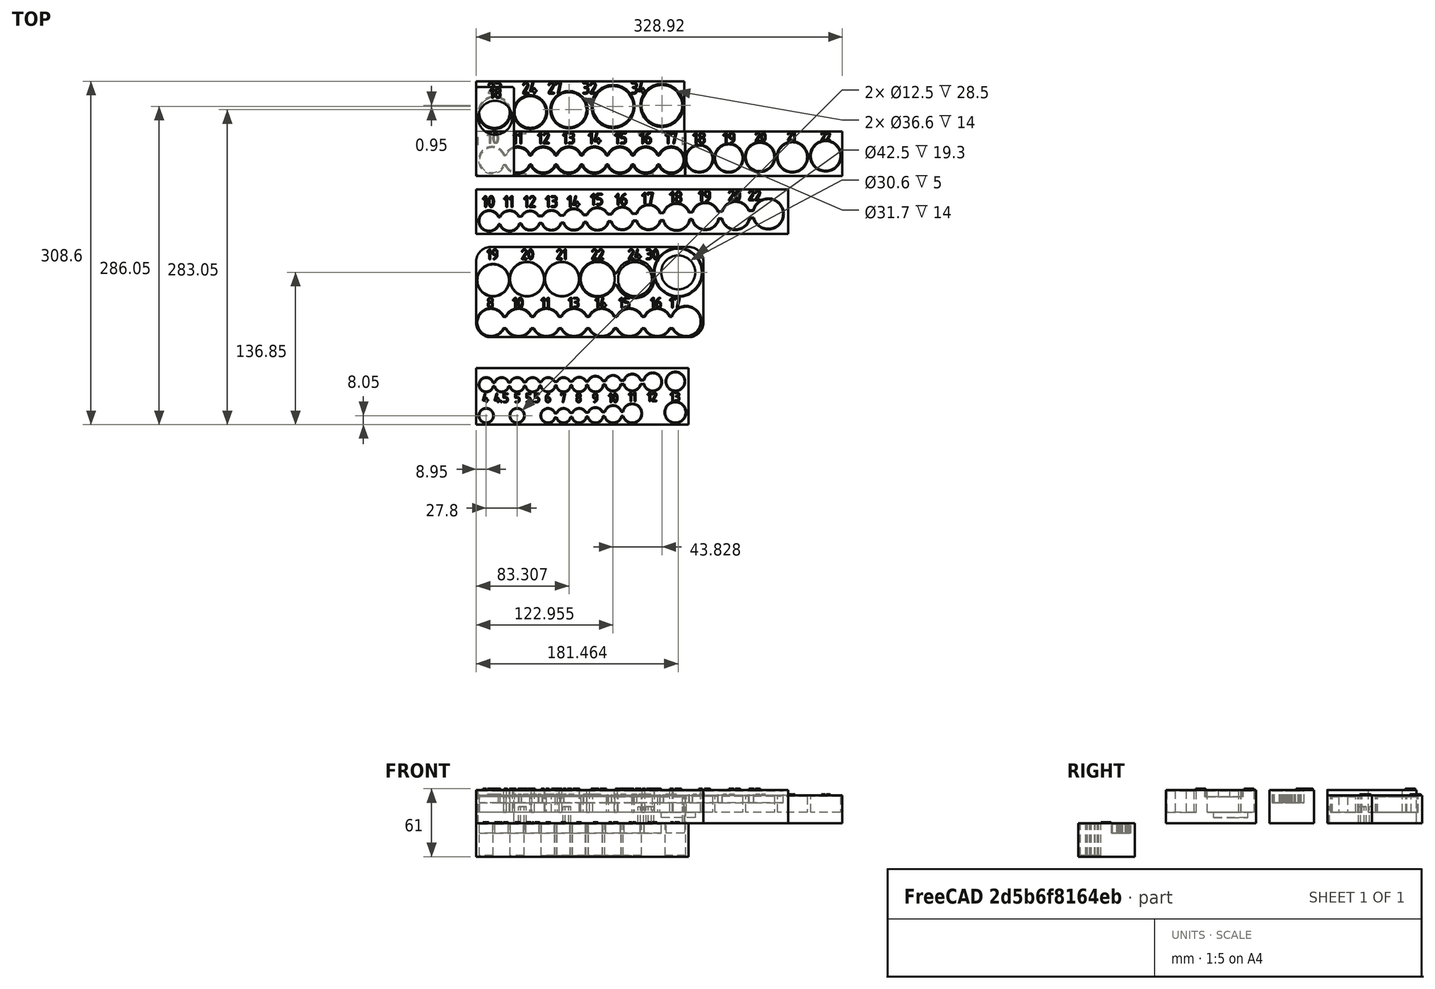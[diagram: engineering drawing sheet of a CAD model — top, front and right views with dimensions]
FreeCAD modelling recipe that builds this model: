
FCSTD DOCUMENT  (FreeCAD 1.1R44227 +568 (Git))
Label: Socket_organizer
License: All rights reserved
LicenseURL: https://en.wikipedia.org/wiki/All_rights_reserved
objects: PartDesign::Pad×64, Part::Part2DObjectPython×57, Sketcher::SketchObject×19, PartDesign::Pocket×15, PartDesign::Chamfer×7, PartDesign::Body×7, App::Point×7, PartDesign::Fillet×3
note: 369 computed .brp shape members not serialized (recipe doc carries the construction recipe); baked Part::Feature solids carry a one-line shape summary decoded from their .brp

FEATURE [Sketcher::SketchObject] Sketch001
  ArcFitTolerance = 1e-06
  ExternalTypes = [0]
  FullyConstrained = true
  MakeInternals = false
  MapMode = 5
  Placement = pos=(0,0,25) rot=(0,0,1;0rad)
  _ExternalGeoVersion = 0
  sketch-geometry (42):
    g0: LineSegment [constr] StartX=14.25 StartY=3 StartZ=0 EndX=14.25 EndY=0 EndZ=0
    g1: LineSegment [constr] StartX=3 StartY=14.25 StartZ=0 EndX=0 EndY=14.25 EndZ=0
    g2: ArcOfCircle CenterX=14.25 CenterY=14.25 CenterZ=0 NormalX=0 NormalY=0 NormalZ=1 AngleXU=0 Radius=11.25 StartAngle=0.363508 EndAngle=5.91968
    g3: LineSegment StartX=24.7649 StartY=18.25 StartZ=0 EndX=26.7351 EndY=18.25 EndZ=0
    g4: LineSegment StartX=24.7649 StartY=10.25 StartZ=0 EndX=26.7351 EndY=10.25 EndZ=0
    g5: ArcOfCircle CenterX=37.25 CenterY=14.25 CenterZ=0 NormalX=0 NormalY=0 NormalZ=1 AngleXU=0 Radius=11.25 StartAngle=0.363508 EndAngle=2.77808
    g6: ArcOfCircle CenterX=37.25 CenterY=14.25 CenterZ=0 NormalX=0 NormalY=0 NormalZ=1 AngleXU=0 Radius=11.25 StartAngle=3.5051 EndAngle=5.91968
    g7: ArcOfCircle CenterX=60.25 CenterY=14.25 CenterZ=0 NormalX=0 NormalY=0 NormalZ=1 AngleXU=0 Radius=11.25 StartAngle=0.363508 EndAngle=2.77808
    g8: ArcOfCircle CenterX=60.25 CenterY=14.25 CenterZ=0 NormalX=0 NormalY=0 NormalZ=1 AngleXU=0 Radius=11.25 StartAngle=3.5051 EndAngle=5.91968
    g9: ArcOfCircle CenterX=83.25 CenterY=14.25 CenterZ=0 NormalX=0 NormalY=0 NormalZ=1 AngleXU=0 Radius=11.25 StartAngle=0.363508 EndAngle=2.77808
    g10: ArcOfCircle CenterX=83.25 CenterY=14.25 CenterZ=0 NormalX=0 NormalY=0 NormalZ=1 AngleXU=0 Radius=11.25 StartAngle=3.5051 EndAngle=5.91968
    g11: ArcOfCircle CenterX=106.25 CenterY=14.25 CenterZ=0 NormalX=0 NormalY=0 NormalZ=1 AngleXU=0 Radius=11.25 StartAngle=0.363508 EndAngle=2.77808
    g12: ArcOfCircle CenterX=106.25 CenterY=14.25 CenterZ=0 NormalX=0 NormalY=0 NormalZ=1 AngleXU=0 Radius=11.25 StartAngle=3.5051 EndAngle=5.91968
    g13: LineSegment StartX=49.7351 StartY=18.25 StartZ=0 EndX=47.7649 EndY=18.25 EndZ=0
    g14: LineSegment StartX=49.7351 StartY=10.25 StartZ=0 EndX=47.7649 EndY=10.25 EndZ=0
    g15: LineSegment StartX=72.7351 StartY=18.25 StartZ=0 EndX=70.7649 EndY=18.25 EndZ=0
    g16: LineSegment StartX=72.7351 StartY=10.25 StartZ=0 EndX=70.7649 EndY=10.25 EndZ=0
    g17: LineSegment StartX=95.7351 StartY=18.25 StartZ=0 EndX=93.7649 EndY=18.25 EndZ=0
    g18: LineSegment StartX=95.7351 StartY=10.25 StartZ=0 EndX=93.7649 EndY=10.25 EndZ=0
    g19: ArcOfCircle CenterX=129.25 CenterY=14.25 CenterZ=0 NormalX=0 NormalY=0 NormalZ=1 AngleXU=0 Radius=11.25 StartAngle=0.363508 EndAngle=2.77808
    g20: ArcOfCircle CenterX=152.25 CenterY=14.25 CenterZ=0 NormalX=0 NormalY=0 NormalZ=1 AngleXU=0 Radius=11.25 StartAngle=0.363508 EndAngle=2.77808
    g21: ArcOfCircle CenterX=129.25 CenterY=14.25 CenterZ=0 NormalX=0 NormalY=0 NormalZ=1 AngleXU=0 Radius=11.25 StartAngle=3.5051 EndAngle=5.91968
    g22: ArcOfCircle CenterX=152.25 CenterY=14.25 CenterZ=0 NormalX=0 NormalY=0 NormalZ=1 AngleXU=0 Radius=11.25 StartAngle=3.5051 EndAngle=5.91968
    g23: LineSegment StartX=164.735 StartY=18.25 StartZ=0 EndX=162.765 EndY=18.25 EndZ=0
    g24: LineSegment StartX=164.735 StartY=10.25 StartZ=0 EndX=162.765 EndY=10.25 EndZ=0
    g25: LineSegment StartX=116.765 StartY=10.25 StartZ=0 EndX=118.735 EndY=10.25 EndZ=0
    g26: LineSegment StartX=118.735 StartY=18.25 StartZ=0 EndX=116.765 EndY=18.25 EndZ=0
    g27: LineSegment StartX=139.765 StartY=18.25 StartZ=0 EndX=141.735 EndY=18.25 EndZ=0
    g28: LineSegment StartX=141.735 StartY=10.25 StartZ=0 EndX=139.765 EndY=10.25 EndZ=0
    g29: ArcOfCircle CenterX=175.25 CenterY=14.25 CenterZ=0 NormalX=0 NormalY=0 NormalZ=1 AngleXU=0 Radius=11.25 StartAngle=3.5051 EndAngle=9.06127
    g30: LineSegment [constr] StartX=14.25 StartY=14.25 StartZ=0 EndX=37.25 EndY=14.25 EndZ=0
    g31: LineSegment [constr] StartX=37.25 StartY=14.25 StartZ=0 EndX=60.25 EndY=14.25 EndZ=0
    g32: LineSegment [constr] StartX=60.25 StartY=14.25 StartZ=0 EndX=83.25 EndY=14.25 EndZ=0
    g33: LineSegment [constr] StartX=83.25 StartY=14.25 StartZ=0 EndX=106.25 EndY=14.25 EndZ=0
    g34: LineSegment [constr] StartX=106.25 StartY=14.25 StartZ=0 EndX=129.25 EndY=14.25 EndZ=0
    g35: LineSegment [constr] StartX=152.25 StartY=14.25 StartZ=0 EndX=129.25 EndY=14.25 EndZ=0
    g36: LineSegment [constr] StartX=152.25 StartY=14.25 StartZ=0 EndX=175.25 EndY=14.25 EndZ=0
    g37: LineSegment StartX=0 StartY=0 StartZ=0 EndX=187.5 EndY=0 EndZ=0
    g38: LineSegment StartX=187.5 StartY=0 StartZ=0 EndX=187.5 EndY=40 EndZ=0
    g39: LineSegment StartX=187.5 StartY=40 StartZ=0 EndX=0 EndY=40 EndZ=0
    g40: LineSegment StartX=0 StartY=40 StartZ=0 EndX=0 EndY=0 EndZ=0
    g41: LineSegment [constr] StartX=187.5 StartY=14.25 StartZ=0 EndX=186.5 EndY=14.25 EndZ=0
  constraints (129):
    c: PointOnObject(g0,g-1)
    c: Vertical(g0)
    c: PointOnObject(g1,g-2)
    c: Horizontal(g1)
    c: Equal(g0,g1)
    c: DistanceY(g0,g0) = 3
    c: PointOnObject(g1,g2)
    c: PointOnObject(g0,g2)
    c: Perpendicular(g2,g0)
    c: Perpendicular(g2,g1)
    c: Coincident(g3,g2)
    c: Horizontal(g3)
    c: Coincident(g4,g2)
    c: Horizontal(g4)
    c: Coincident(g5,g3)
    c: Coincident(g6,g5)
    c: Coincident(g6,g4)
    c: Coincident(g8,g7)
    c: Coincident(g10,g9)
    c: Coincident(g12,g11)
    c: Coincident(g13,g7)
    c: Coincident(g13,g5)
    c: Coincident(g14,g8)
    c: Coincident(g14,g6)
    c: Horizontal(g14)
    c: Coincident(g15,g9)
    c: Coincident(g15,g7)
    c: Coincident(g16,g10)
    c: Coincident(g16,g8)
    c: Coincident(g17,g11)
    c: Coincident(g17,g9)
    c: Coincident(g18,g12)
    c: Coincident(g18,g10)
    c: Coincident(g21,g19)
    c: Coincident(g22,g20)
    c: Equal(g20,g19)
    c: Equal(g19,g11)
    c: Equal(g11,g9)
    c: Equal(g9,g7)
    c: Equal(g7,g5)
    c: Equal(g5,g2)
    c: Equal(g2,g6)
    c: Equal(g6,g8)
    c: Equal(g8,g10)
    c: Equal(g10,g12)
    c: Equal(g12,g21)
    c: Equal(g21,g22)
    c: Coincident(g23,g20)
    c: Coincident(g24,g22)
    c: Coincident(g25,g12)
    c: Coincident(g25,g21)
    c: Coincident(g26,g19)
    c: Coincident(g26,g11)
    c: Diameter(g2) = 22.5
    c: Horizontal(g24)
    c: Horizontal(g23)
    c: Coincident(g27,g19)
    c: Coincident(g27,g20)
    c: Coincident(g28,g22)
    c: Coincident(g28,g21)
    c: Horizontal(g28)
    c: Horizontal(g27)
    c: Horizontal(g25)
    c: Horizontal(g26)
    c: Horizontal(g18)
    c: Horizontal(g17)
    c: Horizontal(g15)
    c: Horizontal(g16)
    c: Horizontal(g13)
    c: Horizontal(g20,g19)
    c: Horizontal(g19,g11)
    c: Horizontal(g11,g9)
    c: Horizontal(g9,g7)
    c: Horizontal(g7,g5)
    c: Horizontal(g5,g2)
    c: Horizontal(g22,g21)
    c: Horizontal(g21,g12)
    c: Horizontal(g12,g10)
    c: Horizontal(g10,g8)
    c: Horizontal(g8,g6)
    c: Horizontal(g6,g2)
    c: Horizontal(g20,g19)
    c: Horizontal(g19,g11)
    c: Horizontal(g11,g9)
    c: Horizontal(g9,g7)
    c: Horizontal(g7,g5)
    c: Horizontal(g5,g2)
    c: Coincident(g29,g23)
    c: Coincident(g29,g24)
    c: Horizontal(g29,g20)
    c: DistanceY(g2,g2) = 4
    c: DistanceY(g2,g2) = 4
    c: Coincident(g30,g2)
    c: Coincident(g30,g5)
    c: Coincident(g31,g5)
    c: Coincident(g31,g7)
    c: Coincident(g32,g7)
    c: Coincident(g32,g9)
    c: Coincident(g33,g9)
    c: Coincident(g33,g11)
    c: Coincident(g34,g11)
    c: Coincident(g34,g19)
    c: Coincident(g35,g20)
    c: Coincident(g35,g19)
    c: Coincident(g36,g20)
    c: Coincident(g36,g29)
    c: Equal(g36,g35)
    c: Equal(g35,g34)
    c: Equal(g34,g33)
    c: Equal(g33,g32)
    c: Equal(g32,g31)
    c: Equal(g31,g30)
    c: Equal(g29,g22)
    c: DistanceX(g30,g30) = 23
    c: Coincident(g37,g38)
    c: Coincident(g38,g39)
    c: Coincident(g39,g40)
    c: Coincident(g40,g37)
    c: Horizontal(g37)
    c: Horizontal(g39)
    c: Vertical(g38)
    c: Vertical(g40)
    c: Coincident(g37,g-1)
    c: DistanceY(g40,g40) = 40
    c: PointOnObject(g41,g38)
    c: PointOnObject(g41,g29)
    c: Horizontal(g41)
    c: Perpendicular(g29,g41)
    c: DistanceX(g41,g41) = 1
FEATURE [PartDesign::Pad] Pad
  Direction = (0,0,1)
  Length = 25
  Length2 = 10
  Placement = pos=(0,0,25) rot=(0,0,1;0rad)
  Profile = -> Sketch001 [Edge32,Edge29,Edge31,Edge30]
  ReferenceAxis = -> Sketch001 [N_Axis]
  Refine = true
  Reversed = true
  SideType = 0
  Suppressed = false
  Type = 0
  Type2 = 0
FEATURE [PartDesign::Pocket] Pocket
  BaseFeature = -> Pad
  Direction = (0,0,-1)
  Length = 15
  Length2 = 5
  Placement = pos=(0,0,25) rot=(0,0,1;0rad)
  Profile = -> Sketch001 [Edge13,Edge12,Edge10,Edge11,Edge9,Vertex8,Edge8,Edge7,Edge14,Edge15,Edge17,Vertex17,Edge16,Edge6,Edge5,Edge4,Edge18,Edge19,Edge3,Edge2,Edge20,Edge21,Edge1,Edge22,Edge28,Edge27,Edge23,Edge25,Edge24,Edge26]
  ReferenceAxis = -> Sketch001 [N_Axis]
  Refine = true
  SideType = 0
  Suppressed = false
  Type = 0
  Type2 = 0
FEATURE [Sketcher::SketchObject] Sketch
  ArcFitTolerance = 1e-06
  AttachmentSupport = -> [XY_Plane001]
  ExternalTypes = [0]
  FullyConstrained = true
  MakeInternals = false
  MapMode = 5
  _ExternalGeoVersion = 0
  sketch-geometry (25):
    g0: LineSegment StartX=0 StartY=0 StartZ=0 EndX=140.921 EndY=0 EndZ=0
    g1: LineSegment StartX=140.921 StartY=0 StartZ=0 EndX=140.921 EndY=40 EndZ=0
    g2: LineSegment StartX=140.921 StartY=40 StartZ=0 EndX=0 EndY=40 EndZ=0
    g3: LineSegment StartX=0 StartY=40 StartZ=0 EndX=0 EndY=0 EndZ=0
    g4: Circle CenterX=12.5 CenterY=15.5 CenterZ=0 NormalX=0 NormalY=0 NormalZ=1 AngleXU=0 Radius=11.8
    g5: Circle CenterX=38.9904 CenterY=16 CenterZ=0 NormalX=0 NormalY=0 NormalZ=1 AngleXU=0 Radius=12.35
    g6: Circle CenterX=67.0011 CenterY=17.05 CenterZ=0 NormalX=0 NormalY=0 NormalZ=1 AngleXU=0 Radius=12.8
    g7: Circle CenterX=96.051 CenterY=17 CenterZ=0 NormalX=0 NormalY=0 NormalZ=1 AngleXU=0 Radius=13.25
    g8: Circle CenterX=125.971 CenterY=17.95 CenterZ=0 NormalX=0 NormalY=0 NormalZ=1 AngleXU=0 Radius=13.3
    g9: Circle [constr] CenterX=12.5 CenterY=15.5 CenterZ=0 NormalX=0 NormalY=0 NormalZ=1 AngleXU=0 Radius=12.5
    g10: Circle [constr] CenterX=38.9904 CenterY=16 CenterZ=0 NormalX=0 NormalY=0 NormalZ=1 AngleXU=0 Radius=13
    g11: Circle [constr] CenterX=67.0011 CenterY=17.05 CenterZ=0 NormalX=0 NormalY=0 NormalZ=1 AngleXU=0 Radius=14.05
    g12: Circle [constr] CenterX=96.051 CenterY=17 CenterZ=0 NormalX=0 NormalY=0 NormalZ=1 AngleXU=0 Radius=14
    g13: Circle [constr] CenterX=125.971 CenterY=17.95 CenterZ=0 NormalX=0 NormalY=0 NormalZ=1 AngleXU=0 Radius=14.95
    g14: LineSegment [constr] StartX=12.5 StartY=3 StartZ=0 EndX=12.5 EndY=0 EndZ=0
    g15: LineSegment [constr] StartX=38.9904 StartY=3 StartZ=0 EndX=38.9904 EndY=0 EndZ=0
    g16: LineSegment [constr] StartX=67.0011 StartY=3 StartZ=0 EndX=67.0011 EndY=0 EndZ=0
    g17: LineSegment [constr] StartX=96.051 StartY=3 StartZ=0 EndX=96.051 EndY=0 EndZ=0
    g18: LineSegment [constr] StartX=125.971 StartY=3 StartZ=0 EndX=125.971 EndY=0 EndZ=0
    g19: LineSegment [constr] StartX=25 StartY=15.5 StartZ=0 EndX=26 EndY=15.5 EndZ=0
    g20: LineSegment [constr] StartX=51.9904 StartY=16 StartZ=0 EndX=52.9904 EndY=16 EndZ=0
    g21: LineSegment [constr] StartX=81.0511 StartY=17.05 StartZ=0 EndX=82.0511 EndY=17.05 EndZ=0
    g22: LineSegment [constr] StartX=110.051 StartY=17 StartZ=0 EndX=111.051 EndY=17 EndZ=0
    g23: GeomPoint [constr] X=0 Y=15.5 Z=0
    g24: GeomPoint [constr] X=140.921 Y=17.95 Z=0
  constraints (76):
    c: Coincident(g0,g1)
    c: Coincident(g1,g2)
    c: Coincident(g2,g3)
    c: Coincident(g3,g0)
    c: Horizontal(g0)
    c: Horizontal(g2)
    c: Vertical(g1)
    c: Vertical(g3)
    c: Coincident(g0,g-1)
    c: Diameter(g4) = 23.6
    c: Diameter(g5) = 24.7
    c: Diameter(g6) = 25.6
    c: Diameter(g7) = 26.5
    c: Diameter(g8) = 26.6
    c: Coincident(g9,g4)
    c: Coincident(g10,g5)
    c: Coincident(g11,g6)
    c: Coincident(g12,g7)
    c: Coincident(g13,g8)
    c: Diameter(g9) = 25
    c: Diameter(g10) = 26
    c: Diameter(g11) = 28.1
    c: Diameter(g12) = 28
    c: Diameter(g13) = 29.9
    c: PointOnObject(g14,g9)
    c: PointOnObject(g14,g0)
    c: Vertical(g14)
    c: PointOnObject(g15,g10)
    c: PointOnObject(g15,g0)
    c: Vertical(g15)
    c: PointOnObject(g16,g11)
    c: PointOnObject(g16,g0)
    c: PointOnObject(g17,g12)
    c: PointOnObject(g17,g0)
    c: Vertical(g17)
    c: PointOnObject(g18,g13)
    c: PointOnObject(g18,g0)
    c: Vertical(g18)
    c: Perpendicular(g13,g18)
    c: Perpendicular(g12,g17)
    c: Vertical(g16)
    c: Perpendicular(g11,g16)
    c: Perpendicular(g10,g15)
    c: Perpendicular(g9,g14)
    c: Equal(g14,g15)
    c: Equal(g15,g16)
    c: Equal(g16,g17)
    c: Equal(g17,g18)
    c: DistanceY(g14,g14) = 3
    c: PointOnObject(g19,g9)
    c: PointOnObject(g19,g10)
    c: Horizontal(g19)
    c: Perpendicular(g9,g19)
    c: PointOnObject(g20,g10)
    c: PointOnObject(g20,g11)
    c: Horizontal(g20)
    c: Perpendicular(g10,g20)
    c: PointOnObject(g21,g11)
    c: PointOnObject(g21,g12)
    c: Horizontal(g21)
    c: Perpendicular(g11,g21)
    c: PointOnObject(g22,g12)
    c: PointOnObject(g22,g13)
    c: Horizontal(g22)
    c: Perpendicular(g12,g22)
    c: Equal(g19,g20)
    c: Equal(g20,g21)
    c: Equal(g21,g22)
    c: DistanceX(g19,g19) = 1
    c: PointOnObject(g23,g3)
    c: PointOnObject(g23,g9)
    c: Horizontal(g23,g4)
    c: PointOnObject(g24,g13)
    c: Horizontal(g24,g8)
    c: PointOnObject(g24,g1)
    c: DistanceY(g1,g1) = 40
FEATURE [PartDesign::Pad] Pad001
  Direction = (0,0,1)
  Length = 25
  Length2 = 10
  Profile = -> Sketch [Edge4,Edge3,Edge1,Edge2]
  ReferenceAxis = -> Sketch [N_Axis]
  Refine = true
  Reversed = true
  SideType = 0
  Suppressed = false
  Type = 0
  Type2 = 0
FEATURE [PartDesign::Pocket] Pocket001
  BaseFeature = -> Pad001
  Direction = (0,0,-1)
  Length = 15
  Length2 = 5
  Profile = -> Sketch [Edge5,Edge6,Edge7,Edge8,Edge9]
  ReferenceAxis = -> Sketch [N_Axis]
  Refine = true
  SideType = 0
  Suppressed = false
  Type = 0
  Type2 = 0
FEATURE [Part::Part2DObjectPython] ShapeString  label="ShapeString10"  # Draft 2D object (typed FeaturePython)
  FontFile = <userpath>/Downloads/osifont-master/osifont-master/osifont.ttf
  Fuse = false
  Justification = 6
  JustificationReference = 0
  KeepLeftMargin = false
  MakeFace = true
  ObliqueAngle = 0
  Placement = pos=(10,29,25) rot=(0,0,1;0rad)
  ScaleToSize = true
  Size = 10
  String = 10
  Tracking = 0
FEATURE [Part::Part2DObjectPython] ShapeString001  # Draft 2D object (typed FeaturePython)
  FontFile = <userpath>/Downloads/osifont-master/osifont-master/osifont.ttf
  Fuse = false
  Justification = 6
  JustificationReference = 0
  KeepLeftMargin = false
  MakeFace = true
  ObliqueAngle = 0
  Placement = pos=(33,29,25) rot=(0,0,1;0rad)
  ScaleToSize = true
  Size = 10
  String = 11
  Tracking = 0
FEATURE [Part::Part2DObjectPython] ShapeString002  # Draft 2D object (typed FeaturePython)
  FontFile = <userpath>/Downloads/osifont-master/osifont-master/osifont.ttf
  Fuse = false
  Justification = 6
  JustificationReference = 0
  KeepLeftMargin = false
  MakeFace = true
  ObliqueAngle = 0
  Placement = pos=(55.5,29,25) rot=(0,0,1;0rad)
  ScaleToSize = true
  Size = 10
  String = 12
  Tracking = 0
FEATURE [Part::Part2DObjectPython] ShapeString003  # Draft 2D object (typed FeaturePython)
  FontFile = <userpath>/Downloads/osifont-master/osifont-master/osifont.ttf
  Fuse = false
  Justification = 6
  JustificationReference = 0
  KeepLeftMargin = false
  MakeFace = true
  ObliqueAngle = 0
  Placement = pos=(78,29,25) rot=(0,0,1;0rad)
  ScaleToSize = true
  Size = 10
  String = 13
  Tracking = 0
FEATURE [Part::Part2DObjectPython] ShapeString004  # Draft 2D object (typed FeaturePython)
  FontFile = <userpath>/Downloads/osifont-master/osifont-master/osifont.ttf
  Fuse = false
  Justification = 6
  JustificationReference = 0
  KeepLeftMargin = false
  MakeFace = true
  ObliqueAngle = 0
  Placement = pos=(101,29,25) rot=(0,0,1;0rad)
  ScaleToSize = true
  Size = 10
  String = 14
  Tracking = 0
FEATURE [Part::Part2DObjectPython] ShapeString005  # Draft 2D object (typed FeaturePython)
  FontFile = <userpath>/Downloads/osifont-master/osifont-master/osifont.ttf
  Fuse = false
  Justification = 6
  JustificationReference = 0
  KeepLeftMargin = false
  MakeFace = true
  ObliqueAngle = 0
  Placement = pos=(124.5,29,25) rot=(0,0,1;0rad)
  ScaleToSize = true
  Size = 10
  String = 15
  Tracking = 0
FEATURE [Part::Part2DObjectPython] ShapeString006  # Draft 2D object (typed FeaturePython)
  FontFile = <userpath>/Downloads/osifont-master/osifont-master/osifont.ttf
  Fuse = false
  Justification = 6
  JustificationReference = 0
  KeepLeftMargin = false
  MakeFace = true
  ObliqueAngle = 0
  Placement = pos=(147,29,25) rot=(0,0,1;0rad)
  ScaleToSize = true
  Size = 10
  String = 16
  Tracking = 0
FEATURE [Part::Part2DObjectPython] ShapeString007  # Draft 2D object (typed FeaturePython)
  FontFile = <userpath>/Downloads/osifont-master/osifont-master/osifont.ttf
  Fuse = false
  Justification = 6
  JustificationReference = 0
  KeepLeftMargin = false
  MakeFace = true
  ObliqueAngle = 0
  Placement = pos=(170,29,25) rot=(0,0,1;0rad)
  ScaleToSize = true
  Size = 10
  String = 17
  Tracking = 0
FEATURE [PartDesign::Pad] Pad004
  BaseFeature = -> Pocket
  Direction = (0,0,1)
  Length = 1
  Length2 = 10
  Placement = pos=(0,0,25) rot=(0,0,1;0rad)
  Profile = -> ShapeString
  ReferenceAxis = -> ShapeString [N_Axis]
  Refine = true
  SideType = 0
  Suppressed = false
  Type = 0
  Type2 = 0
FEATURE [PartDesign::Pad] Pad005
  BaseFeature = -> Pad004
  Direction = (0,0,1)
  Length = 1
  Length2 = 10
  Placement = pos=(0,0,25) rot=(0,0,1;0rad)
  Profile = -> ShapeString001
  ReferenceAxis = -> ShapeString001 [N_Axis]
  Refine = true
  SideType = 0
  Suppressed = false
  Type = 0
  Type2 = 0
FEATURE [PartDesign::Pad] Pad006
  BaseFeature = -> Pad005
  Direction = (0,0,1)
  Length = 1
  Length2 = 10
  Placement = pos=(0,0,25) rot=(0,0,1;0rad)
  Profile = -> ShapeString002
  ReferenceAxis = -> ShapeString002 [N_Axis]
  Refine = true
  SideType = 0
  Suppressed = false
  Type = 0
  Type2 = 0
FEATURE [PartDesign::Pad] Pad007
  BaseFeature = -> Pad006
  Direction = (0,0,1)
  Length = 1
  Length2 = 10
  Placement = pos=(0,0,25) rot=(0,0,1;0rad)
  Profile = -> ShapeString003
  ReferenceAxis = -> ShapeString003 [N_Axis]
  Refine = true
  SideType = 0
  Suppressed = false
  Type = 0
  Type2 = 0
FEATURE [PartDesign::Pad] Pad008
  BaseFeature = -> Pad007
  Direction = (0,0,1)
  Length = 1
  Length2 = 10
  Placement = pos=(0,0,25) rot=(0,0,1;0rad)
  Profile = -> ShapeString004
  ReferenceAxis = -> ShapeString004 [N_Axis]
  Refine = true
  SideType = 0
  Suppressed = false
  Type = 0
  Type2 = 0
FEATURE [PartDesign::Pad] Pad009
  BaseFeature = -> Pad008
  Direction = (0,0,1)
  Length = 1
  Length2 = 10
  Placement = pos=(0,0,25) rot=(0,0,1;0rad)
  Profile = -> ShapeString005
  ReferenceAxis = -> ShapeString005 [N_Axis]
  Refine = true
  SideType = 0
  Suppressed = false
  Type = 0
  Type2 = 0
FEATURE [PartDesign::Pad] Pad010
  BaseFeature = -> Pad009
  Direction = (0,0,1)
  Length = 1
  Length2 = 10
  Placement = pos=(0,0,25) rot=(0,0,1;0rad)
  Profile = -> ShapeString006
  ReferenceAxis = -> ShapeString006 [N_Axis]
  Refine = true
  SideType = 0
  Suppressed = false
  Type = 0
  Type2 = 0
FEATURE [PartDesign::Pad] Pad011
  BaseFeature = -> Pad010
  Direction = (0,0,1)
  Length = 1
  Length2 = 10
  Placement = pos=(0,0,25) rot=(0,0,1;0rad)
  Profile = -> ShapeString007
  ReferenceAxis = -> ShapeString007 [N_Axis]
  Refine = true
  SideType = 0
  Suppressed = false
  Type = 0
  Type2 = 0
FEATURE [Part::Part2DObjectPython] ShapeString008  # Draft 2D object (typed FeaturePython)
  FontFile = <userpath>/Downloads/osifont-master/osifont-master/osifont.ttf
  Fuse = false
  Justification = 6
  JustificationReference = 0
  KeepLeftMargin = false
  MakeFace = true
  ObliqueAngle = 0
  Placement = pos=(7,29,0) rot=(0,0,1;0rad)
  ScaleToSize = true
  Size = 10
  String = 18
  Tracking = 0
FEATURE [Part::Part2DObjectPython] ShapeString009  # Draft 2D object (typed FeaturePython)
  FontFile = <userpath>/Downloads/osifont-master/osifont-master/osifont.ttf
  Fuse = false
  Justification = 6
  JustificationReference = 0
  KeepLeftMargin = false
  MakeFace = true
  ObliqueAngle = 0
  Placement = pos=(34,29,0) rot=(0,0,1;0rad)
  ScaleToSize = true
  Size = 10
  String = 19
  Tracking = 0
FEATURE [Part::Part2DObjectPython] ShapeString010  # Draft 2D object (typed FeaturePython)
  FontFile = <userpath>/Downloads/osifont-master/osifont-master/osifont.ttf
  Fuse = false
  Justification = 6
  JustificationReference = 0
  KeepLeftMargin = false
  MakeFace = true
  ObliqueAngle = 0
  Placement = pos=(63,31,0) rot=(0,0,1;0rad)
  ScaleToSize = true
  Size = 8
  String = 20
  Tracking = 0
FEATURE [Part::Part2DObjectPython] ShapeString011  # Draft 2D object (typed FeaturePython)
  FontFile = <userpath>/Downloads/osifont-master/osifont-master/osifont.ttf
  Fuse = false
  Justification = 6
  JustificationReference = 0
  KeepLeftMargin = false
  MakeFace = true
  ObliqueAngle = 0
  Placement = pos=(92,32,0) rot=(0,0,1;0rad)
  ScaleToSize = true
  Size = 7
  String = 21
  Tracking = 0
FEATURE [Part::Part2DObjectPython] ShapeString012  # Draft 2D object (typed FeaturePython)
  FontFile = <userpath>/Downloads/osifont-master/osifont-master/osifont.ttf
  Fuse = false
  Justification = 6
  JustificationReference = 0
  KeepLeftMargin = false
  MakeFace = true
  ObliqueAngle = 0
  Placement = pos=(122,32,0) rot=(0,0,1;0rad)
  ScaleToSize = true
  Size = 7
  String = 22
  Tracking = 0
FEATURE [PartDesign::Pad] Pad012
  BaseFeature = -> Pocket001
  Direction = (0,0,1)
  Length = 1
  Length2 = 10
  Profile = -> ShapeString008
  ReferenceAxis = -> ShapeString008 [N_Axis]
  Refine = true
  SideType = 0
  Suppressed = false
  Type = 0
  Type2 = 0
FEATURE [PartDesign::Pad] Pad013
  BaseFeature = -> Pad012
  Direction = (0,0,1)
  Length = 1
  Length2 = 10
  Profile = -> ShapeString009
  ReferenceAxis = -> ShapeString009 [N_Axis]
  Refine = true
  SideType = 0
  Suppressed = false
  Type = 0
  Type2 = 0
FEATURE [PartDesign::Pad] Pad014
  BaseFeature = -> Pad013
  Direction = (0,0,1)
  Length = 1
  Length2 = 10
  Profile = -> ShapeString010
  ReferenceAxis = -> ShapeString010 [N_Axis]
  Refine = true
  SideType = 0
  Suppressed = false
  Type = 0
  Type2 = 0
FEATURE [PartDesign::Pad] Pad015
  BaseFeature = -> Pad014
  Direction = (0,0,1)
  Length = 1
  Length2 = 10
  Profile = -> ShapeString011
  ReferenceAxis = -> ShapeString011 [N_Axis]
  Refine = true
  SideType = 0
  Suppressed = false
  Type = 0
  Type2 = 0
FEATURE [PartDesign::Pad] Pad016
  BaseFeature = -> Pad015
  Direction = (0,0,1)
  Length = 1
  Length2 = 10
  Profile = -> ShapeString012
  ReferenceAxis = -> ShapeString012 [N_Axis]
  Refine = true
  SideType = 0
  Suppressed = false
  Type = 0
  Type2 = 0
FEATURE [Sketcher::SketchObject] Sketch004
  ArcFitTolerance = 1e-06
  AttachmentSupport = -> [Pad011]
  ExternalGeometry = -> [Pad011]
  ExternalTypes = [0]
  FullyConstrained = true
  MakeInternals = false
  MapMode = 5
  Placement = pos=(0,0,0) rot=(1,0,0;3.14159rad)
  _ExternalGeoVersion = 0
  sketch-geometry (33):
    g0: LineSegment StartX=0 StartY=-30 StartZ=0 EndX=2 EndY=-28 EndZ=0
    g1: LineSegment StartX=2 StartY=-28 StartZ=0 EndX=2 EndY=-35 EndZ=0
    g2: LineSegment StartX=2 StartY=-35 StartZ=0 EndX=0 EndY=-33 EndZ=0
    g3: LineSegment StartX=0 StartY=-33 StartZ=0 EndX=0 EndY=-30 EndZ=0
    g4: LineSegment StartX=40 StartY=-40 StartZ=0 EndX=38 EndY=-38 EndZ=0
    g5: LineSegment StartX=38 StartY=-38 StartZ=0 EndX=45 EndY=-38 EndZ=0
    g6: LineSegment StartX=45 StartY=-38 StartZ=0 EndX=43 EndY=-40 EndZ=0
    g7: LineSegment StartX=43 StartY=-40 StartZ=0 EndX=40 EndY=-40 EndZ=0
    g8: LineSegment StartX=154.5 StartY=0 StartZ=0 EndX=152.5 EndY=-2 EndZ=0
    g9: LineSegment StartX=152.5 StartY=-2 StartZ=0 EndX=159.5 EndY=-2 EndZ=0
    g10: LineSegment StartX=159.5 StartY=-2 StartZ=0 EndX=157.5 EndY=-2e-16 EndZ=0
    g11: LineSegment StartX=157.5 StartY=-2e-16 StartZ=0 EndX=154.5 EndY=0 EndZ=0
    g12: LineSegment StartX=187.5 StartY=-33 StartZ=0 EndX=187.5 EndY=-30 EndZ=0
    g13: LineSegment StartX=187.5 StartY=-30 StartZ=0 EndX=185.5 EndY=-28 EndZ=0
    g14: LineSegment StartX=185.5 StartY=-28 StartZ=0 EndX=185.5 EndY=-35 EndZ=0
    g15: LineSegment StartX=185.5 StartY=-35 StartZ=0 EndX=187.5 EndY=-33 EndZ=0
    g16: LineSegment [constr] StartX=2 StartY=-31.5 StartZ=0 EndX=0 EndY=-31.5 EndZ=0
    g17: LineSegment StartX=80 StartY=0 StartZ=0 EndX=78 EndY=-2 EndZ=0
    g18: LineSegment StartX=78 StartY=-2 StartZ=0 EndX=85 EndY=-2 EndZ=0
    g19: LineSegment StartX=85 StartY=-2 StartZ=0 EndX=83 EndY=0 EndZ=0
    g20: LineSegment StartX=83 StartY=0 StartZ=0 EndX=80 EndY=0 EndZ=0
    g21: LineSegment StartX=40 StartY=0 StartZ=0 EndX=38 EndY=-2 EndZ=0
    g22: LineSegment StartX=38 StartY=-2 StartZ=0 EndX=45 EndY=-2 EndZ=0
    g23: LineSegment StartX=45 StartY=-2 StartZ=0 EndX=43 EndY=0 EndZ=0
    g24: LineSegment StartX=43 StartY=0 StartZ=0 EndX=40 EndY=0 EndZ=0
    g25: LineSegment StartX=80 StartY=-40 StartZ=0 EndX=78 EndY=-38 EndZ=0
    g26: LineSegment StartX=78 StartY=-38 StartZ=0 EndX=85 EndY=-38 EndZ=0
    g27: LineSegment StartX=85 StartY=-38 StartZ=0 EndX=83 EndY=-40 EndZ=0
    g28: LineSegment StartX=83 StartY=-40 StartZ=0 EndX=80 EndY=-40 EndZ=0
    g29: LineSegment StartX=150.5 StartY=-40 StartZ=0 EndX=152.5 EndY=-38 EndZ=0
    g30: LineSegment StartX=145.5 StartY=-38 StartZ=0 EndX=147.5 EndY=-40 EndZ=0
    g31: LineSegment StartX=147.5 StartY=-40 StartZ=0 EndX=150.5 EndY=-40 EndZ=0
    g32: LineSegment StartX=145.5 StartY=-38 StartZ=0 EndX=152.5 EndY=-38 EndZ=0
  constraints (98):
    c: PointOnObject(g0,g-2)
    c: Coincident(g1,g0)
    c: Coincident(g2,g1)
    c: PointOnObject(g2,g-2)
    c: Coincident(g3,g2)
    c: Coincident(g3,g0)
    c: Vertical(g1)
    c: PointOnObject(g4,g-3)
    c: Coincident(g5,g4)
    c: Horizontal(g5)
    c: Coincident(g6,g5)
    c: PointOnObject(g6,g-3)
    c: Coincident(g7,g6)
    c: Coincident(g7,g4)
    c: PointOnObject(g8,g-1)
    c: Coincident(g9,g8)
    c: Horizontal(g9)
    c: PointOnObject(g10,g-1)
    c: Coincident(g11,g10)
    c: Coincident(g11,g8)
    c: Coincident(g9,g10)
    c: Vertical(g12)
    c: Coincident(g13,g12)
    c: Coincident(g14,g13)
    c: Vertical(g14)
    c: Coincident(g15,g14)
    c: Coincident(g15,g12)
    c: Equal(g12,g7)
    c: Equal(g7,g11)
    c: Equal(g11,g3)
    c: Equal(g5,g1)
    c: Equal(g1,g9)
    c: Equal(g9,g14)
    c: Equal(g0,g10)
    c: Equal(g10,g4)
    c: Equal(g4,g15)
    c: Angle(g0) = 0.785398
    c: Angle(g8) = -2.35619
    c: Angle(g4) = 2.35619
    c: Angle(g15) = 0.785398
    c: Symmetric(g1,g1,g16)
    c: Symmetric(g3,g3,g16)
    c: Horizontal(g16)
    c: DistanceX(g2,g1) = 2
    c: DistanceY(g3,g3) = 3
    c: Vertical(g12,g-3)
    c: PointOnObject(g17,g-1)
    c: Coincident(g18,g17)
    c: Horizontal(g18)
    c: PointOnObject(g19,g-1)
    c: Coincident(g20,g19)
    c: Coincident(g20,g17)
    c: Angle(g17) = -2.35619
    c: Coincident(g18,g19)
    c: Equal(g20,g3)
    c: Equal(g1,g18)
    c: Equal(g0,g17)
    c: PointOnObject(g21,g-1)
    c: Coincident(g22,g21)
    c: Horizontal(g22)
    c: PointOnObject(g23,g-1)
    c: Coincident(g24,g23)
    c: Coincident(g24,g21)
    c: Angle(g21) = -2.35619
    c: Coincident(g22,g23)
    c: Coincident(g26,g25)
    c: Horizontal(g26)
    c: Coincident(g27,g26)
    c: Coincident(g28,g27)
    c: Coincident(g28,g25)
    c: Angle(g25) = 2.35619
    c: PointOnObject(g25,g-3)
    c: PointOnObject(g27,g-3)
    c: Equal(g25,g4)
    c: Equal(g28,g7)
    c: Equal(g26,g5)
    c: Coincident(g31,g30)
    c: Coincident(g31,g29)
    c: PointOnObject(g29,g-3)
    c: PointOnObject(g30,g-3)
    c: Equal(g29,g25)
    c: Equal(g31,g28)
    c: DistanceY(g-3,g2) = 7
    c: Horizontal(g2,g12)
    c: Equal(g24,g7)
    c: Equal(g4,g21)
    c: Equal(g22,g5)
    c: Vertical(g4,g21)
    c: Vertical(g17,g25)
    c: Vertical(g29,g8)
    c: DistanceX(g-3,g4) = 40
    c: DistanceX(g30,g-3) = 40
    c: Coincident(g32,g30)
    c: Coincident(g32,g29)
    c: Horizontal(g32)
    c: Equal(g32,g26)
    c: Angle(g30) = -0.785398
    c: DistanceX(g-3,g25) = 80
FEATURE [PartDesign::Pocket] Pocket004
  BaseFeature = -> Pad011
  Direction = (0,0,1)
  Length = 15
  Length2 = 5
  Placement = pos=(0,0,25) rot=(0,0,1;0rad)
  Profile = -> Sketch004
  ReferenceAxis = -> Sketch004 [N_Axis]
  Refine = true
  SideType = 0
  Suppressed = false
  Type = 0
  Type2 = 0
FEATURE [PartDesign::Chamfer] Chamfer
  Angle = 45
  Base = -> Pocket004 [Edge15,Edge19,Edge17,Edge36,Edge34,Edge38,Edge39,Edge32,Edge30,Edge37,Edge35,Edge28,Edge26,Edge33,Edge31,Edge24,Edge22,Edge29,Edge27,Edge20,Edge25,Edge18,Edge23,Edge16,Edge21,Edge14,Edge12,Edge13]
  BaseFeature = -> Pocket004
  ChamferType = 0
  FlipDirection = false
  Placement = pos=(0,0,25) rot=(0,0,1;0rad)
  Refine = true
  Size = 1
  Size2 = 1
  SupportTransform = false
  Suppressed = false
  UseAllEdges = false
FEATURE [PartDesign::Body] Body  label="1_2in__10-17"
  AllowCompound = false
  Group = -> [Sketch001,Pad,Pocket,ShapeString,ShapeString001,ShapeString002,ShapeString003,ShapeString004,ShapeString005,ShapeString006,ShapeString007,Pad004,Pad005,Pad006,Pad007,Pad008,Pad009,Pad010,Pad011,Sketch004,Pocket004,Chamfer]
  Origin = -> Origin
  Tip = -> Chamfer
FEATURE [PartDesign::Chamfer] Chamfer001
  Angle = 45
  Base = -> Pad016 [Edge12,Edge13,Edge14,Edge15,Edge16]
  BaseFeature = -> Pad016
  ChamferType = 0
  FlipDirection = false
  Refine = true
  Size = 0.7
  Size2 = 1
  SupportTransform = false
  Suppressed = false
  UseAllEdges = false
FEATURE [PartDesign::Body] Body001  label="1_2in__18-22"
  AllowCompound = false
  Group = -> [Sketch,Pad001,Pocket001,ShapeString008,ShapeString009,ShapeString010,ShapeString011,ShapeString012,Pad012,Pad013,Pad014,Pad015,Pad016,Chamfer001]
  Origin = -> Origin001
  Placement = pos=(188,0,25) rot=(0,0,1;0rad)
  Tip = -> Chamfer001
FEATURE [Sketcher::SketchObject] Sketch005
  ArcFitTolerance = 1e-06
  AttachmentSupport = -> [XY_Plane004]
  ExternalTypes = [0]
  FullyConstrained = true
  MakeInternals = false
  MapMode = 5
  _ExternalGeoVersion = 0
  sketch-geometry (4):
    g0: LineSegment StartX=0 StartY=0 StartZ=0 EndX=187 EndY=0 EndZ=0
    g1: LineSegment StartX=187 StartY=0 StartZ=0 EndX=187 EndY=45 EndZ=0
    g2: LineSegment StartX=187 StartY=45 StartZ=0 EndX=0 EndY=45 EndZ=0
    g3: LineSegment StartX=0 StartY=45 StartZ=0 EndX=0 EndY=0 EndZ=0
  constraints (11):
    c: Coincident(g0,g1)
    c: Coincident(g1,g2)
    c: Coincident(g2,g3)
    c: Coincident(g3,g0)
    c: Horizontal(g0)
    c: Horizontal(g2)
    c: Vertical(g1)
    c: Vertical(g3)
    c: Coincident(g0,g-1)
    c: DistanceY(g3,g3) = 45
    c: DistanceX(g2,g2) = 187
FEATURE [PartDesign::Pad] Pad017
  Direction = (0,0,1)
  Length = 25
  Length2 = 10
  Profile = -> Sketch005
  ReferenceAxis = -> Sketch005 [N_Axis]
  Refine = true
  SideType = 0
  Suppressed = false
  Type = 0
  Type2 = 0
FEATURE [Sketcher::SketchObject] Sketch006
  ArcFitTolerance = 1e-06
  AttachmentSupport = -> [Pad017]
  ExternalTypes = [0]
  FullyConstrained = true
  MakeInternals = false
  MapMode = 5
  Placement = pos=(0,0,25) rot=(0,0,1;0rad)
  _ExternalGeoVersion = 0
  sketch-geometry (20):
    g0: Circle CenterX=16.35 CenterY=16.85 CenterZ=0 NormalX=0 NormalY=0 NormalZ=1 AngleXU=0 Radius=13.75
    g1: Circle CenterX=48.5901 CenterY=17.4 CenterZ=0 NormalX=0 NormalY=0 NormalZ=1 AngleXU=0 Radius=14.2
    g2: Circle CenterX=83.3074 CenterY=19.45 CenterZ=0 NormalX=0 NormalY=0 NormalZ=1 AngleXU=0 Radius=15.85
    g3: Circle CenterX=122.955 CenterY=22.45 CenterZ=0 NormalX=0 NormalY=0 NormalZ=1 AngleXU=0 Radius=18.3
    g4: Circle CenterX=166.783 CenterY=23.4 CenterZ=0 NormalX=0 NormalY=0 NormalZ=1 AngleXU=0 Radius=18.3
    g5: Circle [constr] CenterX=16.35 CenterY=16.85 CenterZ=0 NormalX=0 NormalY=0 NormalZ=1 AngleXU=0 Radius=15.35
    g6: Circle [constr] CenterX=48.5901 CenterY=17.4 CenterZ=0 NormalX=0 NormalY=0 NormalZ=1 AngleXU=0 Radius=15.9
    g7: Circle [constr] CenterX=83.3074 CenterY=19.45 CenterZ=0 NormalX=0 NormalY=0 NormalZ=1 AngleXU=0 Radius=17.95
    g8: Circle [constr] CenterX=122.955 CenterY=22.45 CenterZ=0 NormalX=0 NormalY=0 NormalZ=1 AngleXU=0 Radius=20.95
    g9: Circle [constr] CenterX=166.783 CenterY=23.4 CenterZ=0 NormalX=0 NormalY=0 NormalZ=1 AngleXU=0 Radius=21.9
    g10: LineSegment [constr] StartX=16.35 StartY=0 StartZ=0 EndX=16.35 EndY=1.5 EndZ=0
    g11: LineSegment [constr] StartX=48.5901 StartY=0 StartZ=0 EndX=48.5901 EndY=1.5 EndZ=0
    g12: LineSegment [constr] StartX=83.3074 StartY=1.5 StartZ=0 EndX=83.3074 EndY=0 EndZ=0
    g13: LineSegment [constr] StartX=122.955 StartY=1.5 StartZ=0 EndX=122.955 EndY=0 EndZ=0
    g14: LineSegment [constr] StartX=166.783 StartY=1.5 StartZ=0 EndX=166.783 EndY=0 EndZ=0
    g15: LineSegment [constr] StartX=1 StartY=16.85 StartZ=0 EndX=0 EndY=16.85 EndZ=0
    g16: LineSegment [constr] StartX=31.6901 StartY=17.4 StartZ=0 EndX=32.6901 EndY=17.4 EndZ=0
    g17: LineSegment [constr] StartX=64.3574 StartY=19.45 StartZ=0 EndX=65.3574 EndY=19.45 EndZ=0
    g18: LineSegment [constr] StartX=101.005 StartY=22.45 StartZ=0 EndX=102.005 EndY=22.45 EndZ=0
    g19: LineSegment [constr] StartX=143.883 StartY=23.4 StartZ=0 EndX=144.883 EndY=23.4 EndZ=0
  constraints (65):
    c: Coincident(g5,g0)
    c: Coincident(g6,g1)
    c: Coincident(g7,g2)
    c: Coincident(g8,g3)
    c: Coincident(g9,g4)
    c: PointOnObject(g10,g-1)
    c: PointOnObject(g10,g5)
    c: PointOnObject(g11,g-1)
    c: Vertical(g11)
    c: PointOnObject(g11,g6)
    c: PointOnObject(g12,g7)
    c: PointOnObject(g12,g-1)
    c: PointOnObject(g13,g8)
    c: PointOnObject(g13,g-1)
    c: PointOnObject(g14,g9)
    c: PointOnObject(g14,g-1)
    c: Vertical(g14)
    c: Vertical(g13)
    c: Vertical(g12)
    c: Vertical(g10)
    c: Perpendicular(g5,g10)
    c: Perpendicular(g6,g11)
    c: Perpendicular(g7,g12)
    c: Perpendicular(g8,g13)
    c: Perpendicular(g9,g14)
    c: PointOnObject(g15,g5)
    c: PointOnObject(g15,g-2)
    c: Horizontal(g15)
    c: Perpendicular(g5,g15)
    c: PointOnObject(g16,g5)
    c: PointOnObject(g16,g6)
    c: Horizontal(g16)
    c: PointOnObject(g17,g6)
    c: PointOnObject(g17,g7)
    c: Horizontal(g17)
    c: PointOnObject(g18,g7)
    c: PointOnObject(g18,g8)
    c: Horizontal(g18)
    c: Perpendicular(g6,g16)
    c: Perpendicular(g7,g17)
    c: Perpendicular(g8,g18)
    c: PointOnObject(g19,g8)
    c: PointOnObject(g19,g9)
    c: Horizontal(g19)
    c: Perpendicular(g9,g19)
    c: Equal(g19,g18)
    c: Equal(g18,g17)
    c: Equal(g17,g16)
    c: DistanceX(g16,g16) = 1
    c: Equal(g14,g13)
    c: Equal(g13,g12)
    c: Equal(g12,g11)
    c: Equal(g11,g10)
    c: DistanceY(g10,g10) = 1.5
    c: Diameter(g5) = 30.7
    c: Diameter(g0) = 27.5
    c: Diameter(g6) = 31.8
    c: Diameter(g1) = 28.4
    c: Diameter(g7) = 35.9
    c: Diameter(g2) = 31.7
    c: Diameter(g8) = 41.9
    c: Diameter(g3) = 36.6
    c: Diameter(g9) = 43.8
    c: Diameter(g4) = 36.6
    c: DistanceX(g15,g15) = 1
FEATURE [PartDesign::Pocket] Pocket005
  BaseFeature = -> Pad017
  Direction = (0,0,-1)
  Length = 15
  Length2 = 5
  Profile = -> Sketch006
  ReferenceAxis = -> Sketch006 [N_Axis]
  Refine = true
  SideType = 0
  Suppressed = false
  Type = 0
  Type2 = 0
FEATURE [PartDesign::Chamfer] Chamfer002
  Angle = 45
  Base = -> Pocket005 [Edge13,Edge14,Edge15,Edge16,Edge17]
  BaseFeature = -> Pocket005
  ChamferType = 0
  FlipDirection = false
  Refine = true
  Size = 1
  Size2 = 1
  SupportTransform = false
  Suppressed = false
  UseAllEdges = false
FEATURE [Part::Part2DObjectPython] ShapeString013  # Draft 2D object (typed FeaturePython)
  AttachmentOffset = pos=(11,34,0) rot=(0,0,1;0rad)
  AttachmentSupport = -> [Chamfer002]
  FontFile = <userpath>/Downloads/osifont-master/osifont-master/osifont.ttf
  Fuse = false
  Justification = 6
  JustificationReference = 0
  KeepLeftMargin = false
  MakeFace = true
  MapMode = 5
  ObliqueAngle = 0
  Placement = pos=(11,34,25) rot=(0,0,1;0rad)
  ScaleToSize = true
  Size = 10
  String = 23
  Tracking = 0
FEATURE [Part::Part2DObjectPython] ShapeString014  # Draft 2D object (typed FeaturePython)
  AttachmentOffset = pos=(42,34,0) rot=(0,0,1;0rad)
  AttachmentSupport = -> [Chamfer002]
  FontFile = <userpath>/Downloads/osifont-master/osifont-master/osifont.ttf
  Fuse = false
  Justification = 6
  JustificationReference = 0
  KeepLeftMargin = false
  MakeFace = true
  MapMode = 5
  ObliqueAngle = 0
  Placement = pos=(42,34,25) rot=(0,0,1;0rad)
  ScaleToSize = true
  Size = 10
  String = 24
  Tracking = 0
FEATURE [Part::Part2DObjectPython] ShapeString015  # Draft 2D object (typed FeaturePython)
  AttachmentOffset = pos=(65,34,0) rot=(0,0,1;0rad)
  AttachmentSupport = -> [Chamfer002]
  FontFile = <userpath>/Downloads/osifont-master/osifont-master/osifont.ttf
  Fuse = false
  Justification = 6
  JustificationReference = 0
  KeepLeftMargin = false
  MakeFace = true
  MapMode = 5
  ObliqueAngle = 0
  Placement = pos=(65,34,25) rot=(0,0,1;0rad)
  ScaleToSize = true
  Size = 10
  String = 27
  Tracking = 0
FEATURE [Part::Part2DObjectPython] ShapeString016  # Draft 2D object (typed FeaturePython)
  AttachmentOffset = pos=(96,34,0) rot=(0,0,1;0rad)
  AttachmentSupport = -> [Chamfer002]
  FontFile = <userpath>/Downloads/osifont-master/osifont-master/osifont.ttf
  Fuse = false
  Justification = 6
  JustificationReference = 0
  KeepLeftMargin = false
  MakeFace = true
  MapMode = 5
  ObliqueAngle = 0
  Placement = pos=(96,34,25) rot=(0,0,1;0rad)
  ScaleToSize = true
  Size = 10
  String = 32
  Tracking = 0
FEATURE [Part::Part2DObjectPython] ShapeString017  # Draft 2D object (typed FeaturePython)
  AttachmentOffset = pos=(139.5,34,0) rot=(0,0,1;0rad)
  AttachmentSupport = -> [Chamfer002]
  FontFile = <userpath>/Downloads/osifont-master/osifont-master/osifont.ttf
  Fuse = false
  Justification = 6
  JustificationReference = 0
  KeepLeftMargin = false
  MakeFace = true
  MapMode = 5
  ObliqueAngle = 0
  Placement = pos=(139.5,34,25) rot=(0,0,1;0rad)
  ScaleToSize = true
  Size = 10
  String = 34
  Tracking = 0
FEATURE [PartDesign::Pad] Pad018
  BaseFeature = -> Chamfer002
  Direction = (0,0,1)
  Length = 1
  Length2 = 10
  Profile = -> ShapeString013
  ReferenceAxis = -> ShapeString013 [N_Axis]
  Refine = true
  SideType = 0
  Suppressed = false
  Type = 0
  Type2 = 0
FEATURE [PartDesign::Pad] Pad019
  BaseFeature = -> Pad018
  Direction = (0,0,1)
  Length = 1
  Length2 = 10
  Profile = -> ShapeString014
  ReferenceAxis = -> ShapeString014 [N_Axis]
  Refine = true
  SideType = 0
  Suppressed = false
  Type = 0
  Type2 = 0
FEATURE [PartDesign::Pad] Pad020
  BaseFeature = -> Pad019
  Direction = (0,0,1)
  Length = 1
  Length2 = 10
  Profile = -> ShapeString015
  ReferenceAxis = -> ShapeString015 [N_Axis]
  Refine = true
  SideType = 0
  Suppressed = false
  Type = 0
  Type2 = 0
FEATURE [PartDesign::Pad] Pad021
  BaseFeature = -> Pad020
  Direction = (0,0,1)
  Length = 1
  Length2 = 10
  Profile = -> ShapeString016
  ReferenceAxis = -> ShapeString016 [N_Axis]
  Refine = true
  SideType = 0
  Suppressed = false
  Type = 0
  Type2 = 0
FEATURE [PartDesign::Pad] Pad022
  BaseFeature = -> Pad021
  Direction = (0,0,1)
  Length = 1
  Length2 = 10
  Profile = -> ShapeString017
  ReferenceAxis = -> ShapeString017 [N_Axis]
  Refine = true
  SideType = 0
  Suppressed = false
  Type = 0
  Type2 = 0
FEATURE [PartDesign::Body] Body004  label="1_2in__23-34"
  AllowCompound = false
  Group = -> [Sketch005,Pad017,Sketch006,Pocket005,Chamfer002,ShapeString013,ShapeString014,ShapeString015,ShapeString016,ShapeString017,Pad018,Pad019,Pad020,Pad021,Pad022]
  Origin = -> Origin004
  Placement = pos=(0,40,0) rot=(0,0,1;0rad)
  Tip = -> Pad022
FEATURE [Sketcher::SketchObject] Sketch007
  ArcFitTolerance = 1e-06
  AttachmentSupport = -> [XY_Plane005]
  ExternalTypes = [0]
  FullyConstrained = true
  MakeInternals = false
  MapMode = 5
  _ExternalGeoVersion = 0
  sketch-geometry (4):
    g0: LineSegment StartX=0 StartY=0 StartZ=0 EndX=204 EndY=0 EndZ=0
    g1: LineSegment StartX=204 StartY=0 StartZ=0 EndX=204 EndY=81 EndZ=0
    g2: LineSegment StartX=204 StartY=81 StartZ=0 EndX=0 EndY=81 EndZ=0
    g3: LineSegment StartX=0 StartY=81 StartZ=0 EndX=0 EndY=0 EndZ=0
  constraints (11):
    c: Coincident(g0,g1)
    c: Coincident(g1,g2)
    c: Coincident(g2,g3)
    c: Coincident(g3,g0)
    c: Horizontal(g0)
    c: Horizontal(g2)
    c: Vertical(g1)
    c: Vertical(g3)
    c: Coincident(g0,g-1)
    c: DistanceX(g0,g0) = 204
    c: DistanceY(g1,g1) = 81
FEATURE [PartDesign::Pad] Pad023
  Direction = (0,0,1)
  Length = 30
  Length2 = 10
  Profile = -> Sketch007
  ReferenceAxis = -> Sketch007 [N_Axis]
  Refine = true
  SideType = 0
  Suppressed = false
  Type = 0
  Type2 = 0
FEATURE [Sketcher::SketchObject] Sketch008
  ArcFitTolerance = 1e-06
  AttachmentSupport = -> [Pad023]
  ExternalTypes = [0]
  FullyConstrained = true
  MakeInternals = false
  MapMode = 5
  Placement = pos=(0,0,30) rot=(0,0,1;0rad)
  _ExternalGeoVersion = 0
  sketch-geometry (37):
    g0: ArcOfCircle CenterX=13.2 CenterY=13.2 CenterZ=0 NormalX=0 NormalY=0 NormalZ=1 AngleXU=0 Radius=12.2 StartAngle=0.422274 EndAngle=5.86091
    g1: ArcOfCircle CenterX=38.1 CenterY=13.2 CenterZ=0 NormalX=0 NormalY=0 NormalZ=1 AngleXU=0 Radius=12.2 StartAngle=0.422274 EndAngle=2.71932
    g2: ArcOfCircle CenterX=63 CenterY=13.2 CenterZ=0 NormalX=0 NormalY=0 NormalZ=1 AngleXU=0 Radius=12.2 StartAngle=0.422274 EndAngle=2.71932
    g3: ArcOfCircle CenterX=87.9 CenterY=13.2 CenterZ=0 NormalX=0 NormalY=0 NormalZ=1 AngleXU=0 Radius=12.2 StartAngle=0.422274 EndAngle=2.71932
    g4: LineSegment StartX=24.3283 StartY=18.2 StartZ=0 EndX=26.9717 EndY=18.2 EndZ=0
    g5: LineSegment StartX=49.2283 StartY=18.2 StartZ=0 EndX=51.8717 EndY=18.2 EndZ=0
    g6: LineSegment StartX=74.1283 StartY=18.2 StartZ=0 EndX=76.7717 EndY=18.2 EndZ=0
    g7: LineSegment StartX=99.0283 StartY=18.2 StartZ=0 EndX=101.672 EndY=18.2 EndZ=0
    g8: ArcOfCircle CenterX=112.8 CenterY=13.2 CenterZ=0 NormalX=0 NormalY=0 NormalZ=1 AngleXU=0 Radius=12.2 StartAngle=0.422274 EndAngle=2.71932
    g9: LineSegment StartX=123.928 StartY=18.2 StartZ=0 EndX=126.572 EndY=18.2 EndZ=0
    g10: ArcOfCircle CenterX=137.7 CenterY=13.2 CenterZ=0 NormalX=0 NormalY=0 NormalZ=1 AngleXU=0 Radius=12.2 StartAngle=0.422274 EndAngle=2.71932
    g11: LineSegment StartX=148.828 StartY=18.2 StartZ=0 EndX=151.472 EndY=18.2 EndZ=0
    g12: ArcOfCircle CenterX=162.6 CenterY=13.2 CenterZ=0 NormalX=0 NormalY=0 NormalZ=1 AngleXU=0 Radius=12.2 StartAngle=0.422274 EndAngle=2.71932
    g13: LineSegment StartX=173.728 StartY=18.2 StartZ=0 EndX=175.901 EndY=18.2 EndZ=0
    g14: ArcOfCircle CenterX=188.481 CenterY=14.2 CenterZ=0 NormalX=0 NormalY=0 NormalZ=1 AngleXU=0 Radius=13.2 StartAngle=3.61345 EndAngle=9.11691
    g15: LineSegment StartX=24.3283 StartY=8.2 StartZ=0 EndX=26.9717 EndY=8.2 EndZ=0
    g16: ArcOfCircle CenterX=38.1 CenterY=13.2 CenterZ=0 NormalX=0 NormalY=0 NormalZ=1 AngleXU=0 Radius=12.2 StartAngle=3.56387 EndAngle=5.86091
    g17: LineSegment StartX=49.2283 StartY=8.2 StartZ=0 EndX=51.8717 EndY=8.2 EndZ=0
    g18: ArcOfCircle CenterX=63 CenterY=13.2 CenterZ=0 NormalX=0 NormalY=0 NormalZ=1 AngleXU=0 Radius=12.2 StartAngle=3.56387 EndAngle=5.86091
    g19: LineSegment StartX=74.1283 StartY=8.2 StartZ=0 EndX=76.7717 EndY=8.2 EndZ=0
    g20: ArcOfCircle CenterX=87.9 CenterY=13.2 CenterZ=0 NormalX=0 NormalY=0 NormalZ=1 AngleXU=0 Radius=12.2 StartAngle=3.56387 EndAngle=5.86091
    g21: LineSegment StartX=99.0283 StartY=8.2 StartZ=0 EndX=101.672 EndY=8.2 EndZ=0
    g22: ArcOfCircle CenterX=112.8 CenterY=13.2 CenterZ=0 NormalX=0 NormalY=0 NormalZ=1 AngleXU=0 Radius=12.2 StartAngle=3.56387 EndAngle=5.86091
    g23: LineSegment StartX=123.928 StartY=8.2 StartZ=0 EndX=126.572 EndY=8.2 EndZ=0
    g24: ArcOfCircle CenterX=137.7 CenterY=13.2 CenterZ=0 NormalX=0 NormalY=0 NormalZ=1 AngleXU=0 Radius=12.2 StartAngle=3.56387 EndAngle=5.86091
    g25: LineSegment StartX=148.828 StartY=8.2 StartZ=0 EndX=151.472 EndY=8.2 EndZ=0
    g26: ArcOfCircle CenterX=162.6 CenterY=13.2 CenterZ=0 NormalX=0 NormalY=0 NormalZ=1 AngleXU=0 Radius=12.2 StartAngle=3.56387 EndAngle=5.86091
    g27: LineSegment StartX=176.723 StartY=8.2 StartZ=0 EndX=173.728 EndY=8.2 EndZ=0
    g28: LineSegment [constr] StartX=13.2 StartY=0 StartZ=0 EndX=13.2 EndY=1 EndZ=0
    g29: LineSegment [constr] StartX=1 StartY=13.2 StartZ=0 EndX=0 EndY=13.2 EndZ=0
    g30: LineSegment [constr] StartX=188.481 StartY=0 StartZ=0 EndX=188.481 EndY=1 EndZ=0
    g31: Circle [constr] CenterX=13.2 CenterY=13.2 CenterZ=0 NormalX=0 NormalY=0 NormalZ=1 AngleXU=0 Radius=12.2
    g32: Circle [constr] CenterX=38.1 CenterY=13.2 CenterZ=0 NormalX=0 NormalY=0 NormalZ=1 AngleXU=0 Radius=12.2
    g33: LineSegment [constr] StartX=25.4 StartY=13.2 StartZ=0 EndX=25.9 EndY=13.2 EndZ=0
    g34: Circle [constr] CenterX=162.6 CenterY=13.2 CenterZ=0 NormalX=0 NormalY=0 NormalZ=1 AngleXU=0 Radius=12.2
    g35: Circle [constr] CenterX=188.481 CenterY=14.2 CenterZ=0 NormalX=0 NormalY=0 NormalZ=1 AngleXU=0 Radius=13.2
    g36: LineSegment [constr] StartX=174.791 StartY=13.671 StartZ=0 EndX=175.291 EndY=13.6903 EndZ=0
  constraints (120):
    c: Diameter(g0) = 24.4
    c: Vertical(g0,g0)
    c: DistanceY(g0,g0) = 10
    c: Horizontal(g0,g1)
    c: Horizontal(g1,g2)
    c: Horizontal(g2,g3)
    c: Equal(g0,g1)
    c: Equal(g1,g2)
    c: Equal(g2,g3)
    c: Coincident(g4,g0)
    c: Coincident(g4,g1)
    c: Horizontal(g4)
    c: Coincident(g5,g1)
    c: Coincident(g5,g2)
    c: Horizontal(g5)
    c: Horizontal(g1,g1)
    c: Horizontal(g1,g2)
    c: Equal(g4,g5)
    c: Coincident(g6,g2)
    c: Coincident(g6,g3)
    c: Horizontal(g6)
    c: Equal(g6,g5)
    c: Horizontal(g3,g3)
    c: Coincident(g7,g3)
    c: Horizontal(g7)
    c: Coincident(g8,g7)
    c: Equal(g8,g3)
    c: Equal(g7,g6)
    c: Horizontal(g8,g3)
    c: Horizontal(g8,g7)
    c: Coincident(g9,g8)
    c: Horizontal(g9)
    c: Equal(g9,g7)
    c: Coincident(g10,g9)
    c: Horizontal(g10,g9)
    c: Horizontal(g10,g8)
    c: Equal(g10,g8)
    c: Coincident(g11,g10)
    c: Horizontal(g11)
    c: Equal(g11,g9)
    c: Coincident(g12,g11)
    c: Horizontal(g12,g10)
    c: Horizontal(g12,g11)
    c: Equal(g12,g10)
    c: Coincident(g13,g12)
    c: Horizontal(g13)
    c: Coincident(g14,g13)
    c: Diameter(g14) = 26.4
    c: Coincident(g15,g0)
    c: Horizontal(g15)
    c: Coincident(g16,g1)
    c: Coincident(g16,g15)
    c: Equal(g16,g1)
    c: Horizontal(g16,g15)
    c: Coincident(g17,g16)
    c: Horizontal(g17)
    c: Equal(g17,g4)
    c: Coincident(g18,g2)
    c: Coincident(g18,g17)
    c: Horizontal(g18,g17)
    c: Coincident(g19,g18)
    c: Horizontal(g19)
    c: Equal(g19,g6)
    c: Coincident(g20,g3)
    c: Coincident(g20,g19)
    c: Horizontal(g20,g19)
    c: Coincident(g21,g20)
    c: Horizontal(g21)
    c: Equal(g21,g7)
    c: Coincident(g22,g8)
    c: Coincident(g22,g21)
    c: Horizontal(g22,g21)
    c: Coincident(g23,g22)
    c: Horizontal(g23)
    c: Equal(g23,g9)
    c: Coincident(g24,g10)
    c: Coincident(g24,g23)
    c: Horizontal(g24,g23)
    c: Coincident(g25,g24)
    c: Horizontal(g25)
    c: Equal(g25,g11)
    c: Coincident(g26,g12)
    c: Coincident(g26,g25)
    c: Coincident(g27,g14)
    c: Coincident(g27,g26)
    c: PointOnObject(g28,g-1)
    c: PointOnObject(g28,g0)
    c: Vertical(g28)
    c: Perpendicular(g0,g28)
    c: DistanceY(g28,g28) = 1
    c: PointOnObject(g29,g0)
    c: PointOnObject(g29,g-2)
    c: Horizontal(g29)
    c: Perpendicular(g0,g29)
    c: DistanceX(g29,g29) = 1
    c: PointOnObject(g30,g-1)
    c: PointOnObject(g30,g14)
    c: Vertical(g30)
    c: Perpendicular(g14,g30)
    c: DistanceY(g30,g30) = 1
    c: Horizontal(g27)
    c: Coincident(g31,g0)
    c: Equal(g31,g0)
    c: Coincident(g32,g1)
    c: Equal(g32,g1)
    c: PointOnObject(g33,g31)
    c: PointOnObject(g33,g32)
    c: Horizontal(g33)
    c: Perpendicular(g31,g33)
    c: DistanceX(g33,g33) = 0.5
    c: Horizontal(g26,g25)
    c: Coincident(g34,g12)
    c: Equal(g34,g12)
    c: Coincident(g35,g14)
    c: Equal(g35,g14)
    c: PointOnObject(g36,g34)
    c: PointOnObject(g36,g35)
    c: Perpendicular(g34,g36)
    c: Perpendicular(g35,g36)
    c: Distance(g36) = 0.5
FEATURE [PartDesign::Pocket] Pocket006
  BaseFeature = -> Pad023
  Direction = (0,0,-1)
  Length = 20
  Length2 = 5
  Profile = -> Sketch008
  ReferenceAxis = -> Sketch008 [N_Axis]
  Refine = true
  SideType = 0
  Suppressed = false
  Type = 0
  Type2 = 0
FEATURE [Sketcher::SketchObject] Sketch009
  ArcFitTolerance = 1e-06
  AttachmentSupport = -> [Pocket006]
  ExternalTypes = [0]
  FullyConstrained = true
  MakeInternals = false
  MapMode = 5
  Placement = pos=(0,0,30) rot=(0,0,1;0rad)
  _ExternalGeoVersion = 0
  sketch-geometry (20):
    g0: Circle CenterX=15.2 CenterY=51.2 CenterZ=0 NormalX=0 NormalY=0 NormalZ=1 AngleXU=0 Radius=14.2
    g1: Circle CenterX=45.6138 CenterY=52.25 CenterZ=0 NormalX=0 NormalY=0 NormalZ=1 AngleXU=0 Radius=15.25
    g2: Circle CenterX=77.0637 CenterY=52.2 CenterZ=0 NormalX=0 NormalY=0 NormalZ=1 AngleXU=0 Radius=15.2
    g3: Circle CenterX=109.213 CenterY=52.3 CenterZ=0 NormalX=0 NormalY=0 NormalZ=1 AngleXU=0 Radius=15.3
    g4: Circle CenterX=142.663 CenterY=52.25 CenterZ=0 NormalX=0 NormalY=0 NormalZ=1 AngleXU=0 Radius=15.25
    g5: Circle CenterX=181.464 CenterY=58.25 CenterZ=0 NormalX=0 NormalY=0 NormalZ=1 AngleXU=0 Radius=21.25
    g6: LineSegment [constr] StartX=15.2 StartY=37 StartZ=0 EndX=15.2 EndY=0 EndZ=0
    g7: LineSegment [constr] StartX=45.6138 StartY=37 StartZ=0 EndX=45.6138 EndY=0 EndZ=0
    g8: LineSegment [constr] StartX=77.0637 StartY=37 StartZ=0 EndX=77.0637 EndY=0 EndZ=0
    g9: LineSegment [constr] StartX=109.213 StartY=37 StartZ=0 EndX=109.213 EndY=0 EndZ=0
    g10: LineSegment [constr] StartX=142.663 StartY=37 StartZ=0 EndX=142.663 EndY=0 EndZ=0
    g11: LineSegment [constr] StartX=181.464 StartY=37 StartZ=0 EndX=181.464 EndY=0 EndZ=0
    g12: LineSegment [constr] StartX=29.4 StartY=51.2 StartZ=0 EndX=30.4 EndY=51.2 EndZ=0
    g13: LineSegment [constr] StartX=0 StartY=51.2 StartZ=0 EndX=1 EndY=51.2 EndZ=0
    g14: LineSegment [constr] StartX=60.8638 StartY=52.25 StartZ=0 EndX=61.8638 EndY=52.25 EndZ=0
    g15: Circle [constr] CenterX=109.213 CenterY=52.3 CenterZ=0 NormalX=0 NormalY=0 NormalZ=1 AngleXU=0 Radius=15.95
    g16: LineSegment [constr] StartX=92.2637 StartY=52.2 StartZ=0 EndX=93.2637 EndY=52.2 EndZ=0
    g17: Circle [constr] CenterX=142.663 CenterY=52.25 CenterZ=0 NormalX=0 NormalY=0 NormalZ=1 AngleXU=0 Radius=17
    g18: LineSegment [constr] StartX=125.163 StartY=52.3 StartZ=0 EndX=125.663 EndY=52.3 EndZ=0
    g19: LineSegment [constr] StartX=159.464 StartY=54.8479 StartZ=0 EndX=160.464 EndY=55.0026 EndZ=0
  constraints (70):
    c: Diameter(g0) = 28.4
    c: PointOnObject(g6,g0)
    c: PointOnObject(g6,g-1)
    c: Vertical(g6)
    c: Perpendicular(g0,g6)
    c: PointOnObject(g7,g1)
    c: PointOnObject(g7,g-1)
    c: Vertical(g7)
    c: PointOnObject(g8,g2)
    c: PointOnObject(g8,g-1)
    c: Vertical(g8)
    c: PointOnObject(g9,g3)
    c: PointOnObject(g9,g-1)
    c: Vertical(g9)
    c: PointOnObject(g10,g4)
    c: PointOnObject(g10,g-1)
    c: Vertical(g10)
    c: PointOnObject(g11,g5)
    c: PointOnObject(g11,g-1)
    c: Vertical(g11)
    c: Perpendicular(g5,g11)
    c: Perpendicular(g4,g10)
    c: Perpendicular(g3,g9)
    c: Perpendicular(g2,g8)
    c: Equal(g6,g7)
    c: Equal(g7,g8)
    c: Equal(g8,g9)
    c: Equal(g9,g10)
    c: Equal(g10,g11)
    c: DistanceY(g6,g6) = 37
    c: Perpendicular(g1,g7)
    c: PointOnObject(g12,g0)
    c: PointOnObject(g12,g1)
    c: Horizontal(g12)
    c: Perpendicular(g0,g12)
    c: DistanceX(g12,g12) = 1
    c: Diameter(g1) = 30.5
    c: PointOnObject(g13,g-2)
    c: PointOnObject(g13,g0)
    c: Horizontal(g13)
    c: Perpendicular(g0,g13)
    c: DistanceX(g13,g13) = 1
    c: PointOnObject(g14,g1)
    c: PointOnObject(g14,g2)
    c: Horizontal(g14)
    c: Perpendicular(g1,g14)
    c: Equal(g12,g14)
    c: Diameter(g2) = 30.4
    c: Diameter(g3) = 30.6
    c: Coincident(g15,g3)
    c: Diameter(g15) = 31.9
    c: PointOnObject(g16,g2)
    c: PointOnObject(g16,g15)
    c: Horizontal(g16)
    c: Perpendicular(g2,g16)
    c: DistanceX(g16,g16) = 1
    c: Diameter(g4) = 30.5
    c: Coincident(g17,g4)
    c: Diameter(g17) = 34
    c: PointOnObject(g18,g15)
    c: PointOnObject(g18,g17)
    c: Horizontal(g18)
    c: Perpendicular(g15,g18)
    c: DistanceX(g18,g18) = 0.5
    c: Diameter(g5) = 42.5
    c: PointOnObject(g19,g17)
    c: PointOnObject(g19,g5)
    c: Perpendicular(g5,g19)
    c: Perpendicular(g17,g19)
    c: DistanceX(g19,g19) = 1
FEATURE [PartDesign::Pocket] Pocket007
  BaseFeature = -> Pocket006
  Direction = (0,0,-1)
  Length = 20
  Length2 = 5
  Profile = -> Sketch009
  ReferenceAxis = -> Sketch009 [N_Axis]
  Refine = true
  SideType = 0
  Suppressed = false
  Type = 0
  Type2 = 0
FEATURE [PartDesign::Chamfer] Chamfer003
  Angle = 45
  Base = -> Pocket007 [Edge13,Edge17,Edge15,Edge19,Edge21,Edge23,Edge14,Edge16,Edge25,Edge18,Edge27,Edge29,Edge20,Edge31,Edge22,Edge24,Edge33,Edge26,Edge28,Edge35,Edge37,Edge30,Edge32,Edge39,Edge34,Edge36,Edge38,Edge40,Edge46]
  BaseFeature = -> Pocket007
  ChamferType = 0
  FlipDirection = false
  Refine = true
  Size = 0.7
  Size2 = 1
  SupportTransform = false
  Suppressed = false
  UseAllEdges = false
FEATURE [PartDesign::Chamfer] Chamfer004
  Angle = 45
  Base = -> Chamfer003 [Edge33,Edge34,Edge35]
  BaseFeature = -> Chamfer003
  ChamferType = 0
  FlipDirection = false
  Refine = true
  Size = 0.4
  Size2 = 1
  SupportTransform = false
  Suppressed = false
  UseAllEdges = false
FEATURE [PartDesign::Fillet] Fillet
  Base = -> Chamfer004 [Edge97,Edge100,Edge98,Edge102]
  BaseFeature = -> Chamfer004
  Radius = 13
  Refine = true
  SupportTransform = false
  Suppressed = false
  UseAllEdges = false
FEATURE [Part::Part2DObjectPython] ShapeString018  # Draft 2D object (typed FeaturePython)
  AttachmentOffset = pos=(10.5,26.5,0) rot=(0,0,1;0rad)
  AttachmentSupport = -> [Fillet]
  FontFile = <userpath>/Downloads/osifont-master/osifont-master/osifont.ttf
  Fuse = false
  Justification = 6
  JustificationReference = 0
  KeepLeftMargin = false
  MakeFace = true
  MapMode = 5
  ObliqueAngle = 0
  Placement = pos=(10.5,26.5,30) rot=(0,0,1;0rad)
  ScaleToSize = true
  Size = 9
  String = 8
  Tracking = 0
FEATURE [Part::Part2DObjectPython] ShapeString019  # Draft 2D object (typed FeaturePython)
  AttachmentOffset = pos=(33,26.5,0) rot=(0,0,1;0rad)
  AttachmentSupport = -> [Fillet]
  FontFile = <userpath>/Downloads/osifont-master/osifont-master/osifont.ttf
  Fuse = false
  Justification = 6
  JustificationReference = 0
  KeepLeftMargin = false
  MakeFace = true
  MapMode = 5
  ObliqueAngle = 0
  Placement = pos=(33,26.5,30) rot=(0,0,1;0rad)
  ScaleToSize = true
  Size = 9
  String = 10
  Tracking = 0
FEATURE [Part::Part2DObjectPython] ShapeString020  # Draft 2D object (typed FeaturePython)
  AttachmentOffset = pos=(58.5,26.5,0) rot=(0,0,1;0rad)
  AttachmentSupport = -> [Fillet]
  FontFile = <userpath>/Downloads/osifont-master/osifont-master/osifont.ttf
  Fuse = false
  Justification = 6
  JustificationReference = 0
  KeepLeftMargin = false
  MakeFace = true
  MapMode = 5
  ObliqueAngle = 0
  Placement = pos=(58.5,26.5,30) rot=(0,0,1;0rad)
  ScaleToSize = true
  Size = 9
  String = 11
  Tracking = 0
FEATURE [Part::Part2DObjectPython] ShapeString021  # Draft 2D object (typed FeaturePython)
  AttachmentOffset = pos=(83,26.5,0) rot=(0,0,1;0rad)
  AttachmentSupport = -> [Fillet]
  FontFile = <userpath>/Downloads/osifont-master/osifont-master/osifont.ttf
  Fuse = false
  Justification = 6
  JustificationReference = 0
  KeepLeftMargin = false
  MakeFace = true
  MapMode = 5
  ObliqueAngle = 0
  Placement = pos=(83,26.5,30) rot=(0,0,1;0rad)
  ScaleToSize = true
  Size = 9
  String = 13
  Tracking = 0
FEATURE [Part::Part2DObjectPython] ShapeString022  # Draft 2D object (typed FeaturePython)
  AttachmentOffset = pos=(107,26.5,0) rot=(0,0,1;0rad)
  AttachmentSupport = -> [Fillet]
  FontFile = <userpath>/Downloads/osifont-master/osifont-master/osifont.ttf
  Fuse = false
  Justification = 6
  JustificationReference = 0
  KeepLeftMargin = false
  MakeFace = true
  MapMode = 5
  ObliqueAngle = 0
  Placement = pos=(107,26.5,30) rot=(0,0,1;0rad)
  ScaleToSize = true
  Size = 9
  String = 14
  Tracking = 0
FEATURE [Part::Part2DObjectPython] ShapeString023  # Draft 2D object (typed FeaturePython)
  AttachmentOffset = pos=(128.5,26.5,0) rot=(0,0,1;0rad)
  AttachmentSupport = -> [Fillet]
  FontFile = <userpath>/Downloads/osifont-master/osifont-master/osifont.ttf
  Fuse = false
  Justification = 6
  JustificationReference = 0
  KeepLeftMargin = false
  MakeFace = true
  MapMode = 5
  ObliqueAngle = 0
  Placement = pos=(128.5,26.5,30) rot=(0,0,1;0rad)
  ScaleToSize = true
  Size = 9
  String = 15
  Tracking = 0
FEATURE [Part::Part2DObjectPython] ShapeString024  # Draft 2D object (typed FeaturePython)
  AttachmentOffset = pos=(157,26.5,0) rot=(0,0,1;0rad)
  AttachmentSupport = -> [Fillet]
  FontFile = <userpath>/Downloads/osifont-master/osifont-master/osifont.ttf
  Fuse = false
  Justification = 6
  JustificationReference = 0
  KeepLeftMargin = false
  MakeFace = true
  MapMode = 5
  ObliqueAngle = 0
  Placement = pos=(157,26.5,30) rot=(0,0,1;0rad)
  ScaleToSize = true
  Size = 9
  String = 16
  Tracking = 0
FEATURE [Part::Part2DObjectPython] ShapeString025  # Draft 2D object (typed FeaturePython)
  AttachmentOffset = pos=(174,26.5,0) rot=(0,0,1;0rad)
  AttachmentSupport = -> [Fillet]
  FontFile = <userpath>/Downloads/osifont-master/osifont-master/osifont.ttf
  Fuse = false
  Justification = 6
  JustificationReference = 0
  KeepLeftMargin = false
  MakeFace = true
  MapMode = 5
  ObliqueAngle = 0
  Placement = pos=(174,26.5,30) rot=(0,0,1;0rad)
  ScaleToSize = true
  Size = 9
  String = 17
  Tracking = 0
FEATURE [Part::Part2DObjectPython] ShapeString026  # Draft 2D object (typed FeaturePython)
  AttachmentOffset = pos=(10,70,0) rot=(0,0,1;0rad)
  AttachmentSupport = -> [Fillet]
  FontFile = <userpath>/Downloads/osifont-master/osifont-master/osifont.ttf
  Fuse = false
  Justification = 6
  JustificationReference = 0
  KeepLeftMargin = false
  MakeFace = true
  MapMode = 5
  ObliqueAngle = 0
  Placement = pos=(10,70,30) rot=(0,0,1;0rad)
  ScaleToSize = true
  Size = 9
  String = 19
  Tracking = 0
FEATURE [Part::Part2DObjectPython] ShapeString027  # Draft 2D object (typed FeaturePython)
  AttachmentOffset = pos=(41,70,0) rot=(0,0,1;0rad)
  AttachmentSupport = -> [Fillet]
  FontFile = <userpath>/Downloads/osifont-master/osifont-master/osifont.ttf
  Fuse = false
  Justification = 6
  JustificationReference = 0
  KeepLeftMargin = false
  MakeFace = true
  MapMode = 5
  ObliqueAngle = 0
  Placement = pos=(41,70,30) rot=(0,0,1;0rad)
  ScaleToSize = true
  Size = 9
  String = 20
  Tracking = 0
FEATURE [Part::Part2DObjectPython] ShapeString028  # Draft 2D object (typed FeaturePython)
  AttachmentOffset = pos=(72.5,70,0) rot=(0,0,1;0rad)
  AttachmentSupport = -> [Fillet]
  FontFile = <userpath>/Downloads/osifont-master/osifont-master/osifont.ttf
  Fuse = false
  Justification = 6
  JustificationReference = 0
  KeepLeftMargin = false
  MakeFace = true
  MapMode = 5
  ObliqueAngle = 0
  Placement = pos=(72.5,70,30) rot=(0,0,1;0rad)
  ScaleToSize = true
  Size = 9
  String = 21
  Tracking = 0
FEATURE [Part::Part2DObjectPython] ShapeString029  # Draft 2D object (typed FeaturePython)
  AttachmentOffset = pos=(104,70,0) rot=(0,0,1;0rad)
  AttachmentSupport = -> [Fillet]
  FontFile = <userpath>/Downloads/osifont-master/osifont-master/osifont.ttf
  Fuse = false
  Justification = 6
  JustificationReference = 0
  KeepLeftMargin = false
  MakeFace = true
  MapMode = 5
  ObliqueAngle = 0
  Placement = pos=(104,70,30) rot=(0,0,1;0rad)
  ScaleToSize = true
  Size = 9
  String = 22
  Tracking = 0
FEATURE [Part::Part2DObjectPython] ShapeString030  # Draft 2D object (typed FeaturePython)
  AttachmentOffset = pos=(137,70,0) rot=(0,0,1;0rad)
  AttachmentSupport = -> [Fillet]
  FontFile = <userpath>/Downloads/osifont-master/osifont-master/osifont.ttf
  Fuse = false
  Justification = 6
  JustificationReference = 0
  KeepLeftMargin = false
  MakeFace = true
  MapMode = 5
  ObliqueAngle = 0
  Placement = pos=(137,70,30) rot=(0,0,1;0rad)
  ScaleToSize = true
  Size = 9
  String = 24
  Tracking = 0
FEATURE [Part::Part2DObjectPython] ShapeString031  # Draft 2D object (typed FeaturePython)
  AttachmentOffset = pos=(153,70,0) rot=(0,0,1;0rad)
  AttachmentSupport = -> [Fillet]
  FontFile = <userpath>/Downloads/osifont-master/osifont-master/osifont.ttf
  Fuse = false
  Justification = 6
  JustificationReference = 0
  KeepLeftMargin = false
  MakeFace = true
  MapMode = 5
  ObliqueAngle = 0
  Placement = pos=(153,70,30) rot=(0,0,1;0rad)
  ScaleToSize = true
  Size = 9
  String = 30
  Tracking = 0
FEATURE [PartDesign::Pad] Pad024
  BaseFeature = -> Fillet
  Direction = (0,0,1)
  Length = 1
  Length2 = 10
  Profile = -> ShapeString018
  ReferenceAxis = -> ShapeString018 [N_Axis]
  Refine = true
  SideType = 0
  Suppressed = false
  Type = 0
  Type2 = 0
FEATURE [PartDesign::Pad] Pad025
  BaseFeature = -> Pad024
  Direction = (0,0,1)
  Length = 1
  Length2 = 10
  Profile = -> ShapeString019
  ReferenceAxis = -> ShapeString019 [N_Axis]
  Refine = true
  SideType = 0
  Suppressed = false
  Type = 0
  Type2 = 0
FEATURE [PartDesign::Pad] Pad026
  BaseFeature = -> Pad025
  Direction = (0,0,1)
  Length = 1
  Length2 = 10
  Profile = -> ShapeString020
  ReferenceAxis = -> ShapeString020 [N_Axis]
  Refine = true
  SideType = 0
  Suppressed = false
  Type = 0
  Type2 = 0
FEATURE [PartDesign::Pad] Pad027
  BaseFeature = -> Pad026
  Direction = (0,0,1)
  Length = 1
  Length2 = 10
  Profile = -> ShapeString021
  ReferenceAxis = -> ShapeString021 [N_Axis]
  Refine = true
  SideType = 0
  Suppressed = false
  Type = 0
  Type2 = 0
FEATURE [PartDesign::Pad] Pad028
  BaseFeature = -> Pad027
  Direction = (0,0,1)
  Length = 1
  Length2 = 10
  Profile = -> ShapeString022
  ReferenceAxis = -> ShapeString022 [N_Axis]
  Refine = true
  SideType = 0
  Suppressed = false
  Type = 0
  Type2 = 0
FEATURE [PartDesign::Pad] Pad029
  BaseFeature = -> Pad028
  Direction = (0,0,1)
  Length = 1
  Length2 = 10
  Profile = -> ShapeString023
  ReferenceAxis = -> ShapeString023 [N_Axis]
  Refine = true
  SideType = 0
  Suppressed = false
  Type = 0
  Type2 = 0
FEATURE [PartDesign::Pad] Pad030
  BaseFeature = -> Pad029
  Direction = (0,0,1)
  Length = 1
  Length2 = 10
  Profile = -> ShapeString024
  ReferenceAxis = -> ShapeString024 [N_Axis]
  Refine = true
  SideType = 0
  Suppressed = false
  Type = 0
  Type2 = 0
FEATURE [PartDesign::Pad] Pad031
  BaseFeature = -> Pad030
  Direction = (0,0,1)
  Length = 1
  Length2 = 10
  Profile = -> ShapeString025
  ReferenceAxis = -> ShapeString025 [N_Axis]
  Refine = true
  SideType = 0
  Suppressed = false
  Type = 0
  Type2 = 0
FEATURE [PartDesign::Pad] Pad032
  BaseFeature = -> Pad031
  Direction = (0,0,1)
  Length = 1
  Length2 = 10
  Profile = -> ShapeString026
  ReferenceAxis = -> ShapeString026 [N_Axis]
  Refine = true
  SideType = 0
  Suppressed = false
  Type = 0
  Type2 = 0
FEATURE [PartDesign::Pad] Pad033
  BaseFeature = -> Pad032
  Direction = (0,0,1)
  Length = 1
  Length2 = 10
  Profile = -> ShapeString027
  ReferenceAxis = -> ShapeString027 [N_Axis]
  Refine = true
  SideType = 0
  Suppressed = false
  Type = 0
  Type2 = 0
FEATURE [PartDesign::Pad] Pad034
  BaseFeature = -> Pad033
  Direction = (0,0,1)
  Length = 1
  Length2 = 10
  Profile = -> ShapeString028
  ReferenceAxis = -> ShapeString028 [N_Axis]
  Refine = true
  SideType = 0
  Suppressed = false
  Type = 0
  Type2 = 0
FEATURE [PartDesign::Pad] Pad035
  BaseFeature = -> Pad034
  Direction = (0,0,1)
  Length = 1
  Length2 = 10
  Profile = -> ShapeString029
  ReferenceAxis = -> ShapeString029 [N_Axis]
  Refine = true
  SideType = 0
  Suppressed = false
  Type = 0
  Type2 = 0
FEATURE [PartDesign::Pad] Pad036
  BaseFeature = -> Pad035
  Direction = (0,0,1)
  Length = 1
  Length2 = 10
  Profile = -> ShapeString030
  ReferenceAxis = -> ShapeString030 [N_Axis]
  Refine = true
  SideType = 0
  Suppressed = false
  Type = 0
  Type2 = 0
FEATURE [PartDesign::Pad] Pad037
  BaseFeature = -> Pad036
  Direction = (0,0,1)
  Length = 1
  Length2 = 10
  Profile = -> ShapeString031
  ReferenceAxis = -> ShapeString031 [N_Axis]
  Refine = true
  SideType = 0
  Suppressed = false
  Type = 0
  Type2 = 0
FEATURE [Sketcher::SketchObject] Sketch010
  ArcFitTolerance = 1e-06
  AttachmentSupport = -> [Pad037]
  ExternalGeometry = -> [Pad037]
  ExternalTypes = [0]
  FullyConstrained = true
  MakeInternals = false
  MapMode = 5
  Placement = pos=(0,0,10) rot=(0,0,1;0rad)
  _ExternalGeoVersion = 0
  sketch-geometry (1):
    g0: Circle CenterX=181.464 CenterY=58.25 CenterZ=0 NormalX=0 NormalY=0 NormalZ=1 AngleXU=0 Radius=15.3
  constraints (2):
    c: Coincident(g0,g-3)
    c: Diameter(g0) = 30.6
FEATURE [PartDesign::Pocket] Pocket008
  BaseFeature = -> Pad037
  Direction = (0,0,-1)
  Length = 5
  Length2 = 5
  Profile = -> Sketch010
  ReferenceAxis = -> Sketch010 [N_Axis]
  Refine = true
  SideType = 0
  Suppressed = false
  Type = 0
  Type2 = 0
FEATURE [Sketcher::SketchObject] Sketch011
  ArcFitTolerance = 1e-06
  AttachmentSupport = -> [Pocket008]
  ExternalGeometry = -> [Pocket008]
  ExternalTypes = [0]
  FullyConstrained = true
  MakeInternals = false
  MapMode = 5
  Placement = pos=(0,0,30) rot=(0,0,1;0rad)
  _ExternalGeoVersion = 0
  sketch-geometry (6):
    g0: Circle [constr] CenterX=109.213 CenterY=52.3 CenterZ=0 NormalX=0 NormalY=0 NormalZ=1 AngleXU=0 Radius=16.25
    g1: Circle [constr] CenterX=142.663 CenterY=52.25 CenterZ=0 NormalX=0 NormalY=0 NormalZ=1 AngleXU=0 Radius=17.25
    g2: ArcOfCircle CenterX=109.213 CenterY=52.3 CenterZ=0 NormalX=0 NormalY=0 NormalZ=1 AngleXU=0 Radius=16.25 StartAngle=0.363603 EndAngle=5.91958
    g3: ArcOfCircle CenterX=142.663 CenterY=52.25 CenterZ=0 NormalX=0 NormalY=0 NormalZ=1 AngleXU=0 Radius=17.25 StartAngle=3.4816 EndAngle=9.07895
    g4: ArcOfCircle CenterX=125.414 CenterY=58.4648 CenterZ=0 NormalX=0 NormalY=0 NormalZ=1 AngleXU=0 Radius=1.08434 StartAngle=3.5052 EndAngle=5.93736
    g5: ArcOfCircle CenterX=125.397 CenterY=46.1419 CenterZ=0 NormalX=0 NormalY=0 NormalZ=1 AngleXU=0 Radius=1.06524 StartAngle=0.340009 EndAngle=2.77799
  constraints (14):
    c: Coincident(g0,g-3)
    c: Coincident(g1,g-4)
    c: Diameter(g0) = 32.5
    c: Diameter(g1) = 34.5
    c: Coincident(g2,g0)
    c: PointOnObject(g2,g0)
    c: Coincident(g3,g1)
    c: PointOnObject(g3,g1)
    c: Vertical(g2,g2)
    c: Tangent(g4,g3) = 1.5708
    c: Tangent(g4,g2) = 1.5708
    c: Tangent(g5,g2) = 1.5708
    c: Tangent(g5,g3) = 1.5708
    c: Distance(g2,g3) = 2
FEATURE [PartDesign::Pocket] Pocket009
  BaseFeature = -> Pocket008
  Direction = (0,0,-1)
  Length = 6
  Length2 = 5
  Profile = -> Sketch011
  ReferenceAxis = -> Sketch011 [N_Axis]
  Refine = true
  SideType = 0
  Suppressed = false
  Type = 0
  Type2 = 0
FEATURE [PartDesign::Body] Body005  label="pwr_socket"
  AllowCompound = false
  Group = -> [Sketch007,Pad023,Sketch008,Pocket006,Sketch009,Pocket007,Chamfer003,Chamfer004,Fillet,ShapeString018,ShapeString019,ShapeString020,ShapeString021,ShapeString022,ShapeString023,ShapeString024,ShapeString025,ShapeString026,ShapeString027,ShapeString028,ShapeString029,ShapeString030,ShapeString031,Pad024,Pad025,Pad026,Pad027,Pad028,Pad029,Pad030,Pad031,Pad032,Pad033,Pad034,Pad035,Pad036,Pad037,+4 more]
  Origin = -> Origin005
  Placement = pos=(0,-145,0) rot=(0,0,1;0rad)
  Tip = -> Pocket009
FEATURE [Sketcher::SketchObject] Sketch012
  ArcFitTolerance = 1e-06
  AttachmentSupport = -> [XY_Plane006]
  ExternalTypes = [0]
  FullyConstrained = true
  MakeInternals = false
  MapMode = 5
  _ExternalGeoVersion = 0
  sketch-geometry (4):
    g0: LineSegment StartX=0 StartY=0 StartZ=0 EndX=280.29 EndY=0 EndZ=0
    g1: LineSegment StartX=280.29 StartY=0 StartZ=0 EndX=280.29 EndY=40 EndZ=0
    g2: LineSegment StartX=280.29 StartY=40 StartZ=0 EndX=0 EndY=40 EndZ=0
    g3: LineSegment StartX=0 StartY=40 StartZ=0 EndX=0 EndY=0 EndZ=0
  constraints (11):
    c: Coincident(g0,g1)
    c: Coincident(g1,g2)
    c: Coincident(g2,g3)
    c: Coincident(g3,g0)
    c: Horizontal(g0)
    c: Horizontal(g2)
    c: Vertical(g1)
    c: Vertical(g3)
    c: Coincident(g0,g-1)
    c: DistanceY(g3,g3) = 40
    c: DistanceX(g0,g0) = 280.29
FEATURE [PartDesign::Pad] Pad038
  Direction = (0,0,1)
  Length = 30
  Length2 = 10
  Profile = -> Sketch012
  ReferenceAxis = -> Sketch012 [N_Axis]
  Refine = true
  SideType = 0
  Suppressed = false
  Type = 0
  Type2 = 0
FEATURE [Sketcher::SketchObject] Sketch013
  ArcFitTolerance = 1e-06
  AttachmentSupport = -> [Pad038]
  ExternalTypes = [0]
  FullyConstrained = true
  MakeInternals = false
  MapMode = 5
  Placement = pos=(0,0,30) rot=(0,0,1;0rad)
  _ExternalGeoVersion = 0
  sketch-geometry (49):
    g0: Circle [constr] CenterX=11.65 CenterY=11.65 CenterZ=0 NormalX=0 NormalY=0 NormalZ=1 AngleXU=0 Radius=8.65
    g1: Circle [constr] CenterX=29.95 CenterY=11.65 CenterZ=0 NormalX=0 NormalY=0 NormalZ=1 AngleXU=0 Radius=8.65
    g2: Circle [constr] CenterX=48.5476 CenterY=11.95 CenterZ=0 NormalX=0 NormalY=0 NormalZ=1 AngleXU=0 Radius=8.95
    g3: Circle [constr] CenterX=67.6465 CenterY=12.15 CenterZ=0 NormalX=0 NormalY=0 NormalZ=1 AngleXU=0 Radius=9.15
    g4: Circle [constr] CenterX=87.6825 CenterY=12.9 CenterZ=0 NormalX=0 NormalY=0 NormalZ=1 AngleXU=0 Radius=9.9
    g5: Circle [constr] CenterX=108.928 CenterY=13.35 CenterZ=0 NormalX=0 NormalY=0 NormalZ=1 AngleXU=0 Radius=10.35
    g6: Circle [constr] CenterX=131.122 CenterY=13.85 CenterZ=0 NormalX=0 NormalY=0 NormalZ=1 AngleXU=0 Radius=10.85
    g7: Circle [constr] CenterX=154.849 CenterY=14.9 CenterZ=0 NormalX=0 NormalY=0 NormalZ=1 AngleXU=0 Radius=11.9
    g8: LineSegment [constr] StartX=20.3 StartY=11.65 StartZ=0 EndX=21.3 EndY=11.65 EndZ=0
    g9: LineSegment [constr] StartX=38.5989 StartY=11.7895 StartZ=0 EndX=39.5987 EndY=11.8056 EndZ=0
    g10: LineSegment [constr] StartX=57.4971 StartY=12.0437 StartZ=0 EndX=58.497 EndY=12.0542 EndZ=0
    g11: LineSegment [constr] StartX=76.7901 StartY=12.4923 StartZ=0 EndX=77.7894 EndY=12.5297 EndZ=0
    g12: LineSegment [constr] StartX=97.5803 StartY=13.1096 StartZ=0 EndX=98.5801 EndY=13.1308 EndZ=0
    g13: LineSegment [constr] StartX=119.275 StartY=13.5831 StartZ=0 EndX=120.275 EndY=13.6056 EndZ=0
    g14: LineSegment [constr] StartX=141.961 StartY=14.3297 StartZ=0 EndX=142.961 EndY=14.3739 EndZ=0
    g15: LineSegment [constr] StartX=11.65 StartY=0 StartZ=0 EndX=11.65 EndY=3 EndZ=0
    g16: LineSegment [constr] StartX=29.95 StartY=0 StartZ=0 EndX=29.95 EndY=3 EndZ=0
    g17: LineSegment [constr] StartX=48.5476 StartY=0 StartZ=0 EndX=48.5476 EndY=3 EndZ=0
    g18: LineSegment [constr] StartX=67.6465 StartY=0 StartZ=0 EndX=67.6465 EndY=3 EndZ=0
    g19: LineSegment [constr] StartX=87.6825 StartY=0 StartZ=0 EndX=87.6825 EndY=3 EndZ=0
    g20: LineSegment [constr] StartX=108.928 StartY=0 StartZ=0 EndX=108.928 EndY=3 EndZ=0
    g21: LineSegment [constr] StartX=131.122 StartY=0 StartZ=0 EndX=131.122 EndY=3 EndZ=0
    g22: LineSegment [constr] StartX=154.849 StartY=0 StartZ=0 EndX=154.849 EndY=3 EndZ=0
    g23: LineSegment [constr] StartX=3 StartY=11.65 StartZ=0 EndX=0 EndY=11.65 EndZ=0
    g24: Circle [constr] CenterX=179.898 CenterY=15.15 CenterZ=0 NormalX=0 NormalY=0 NormalZ=1 AngleXU=0 Radius=12.15
    g25: Circle [constr] CenterX=205.888 CenterY=15.85 CenterZ=0 NormalX=0 NormalY=0 NormalZ=1 AngleXU=0 Radius=12.85
    g26: Circle [constr] CenterX=233.133 CenterY=16.4 CenterZ=0 NormalX=0 NormalY=0 NormalZ=1 AngleXU=0 Radius=13.4
    g27: Circle [constr] CenterX=262.394 CenterY=17.9 CenterZ=0 NormalX=0 NormalY=0 NormalZ=1 AngleXU=0 Radius=14.9
    g28: LineSegment [constr] StartX=179.898 StartY=0 StartZ=0 EndX=179.898 EndY=3 EndZ=0
    g29: LineSegment [constr] StartX=205.888 StartY=0 StartZ=0 EndX=205.888 EndY=3 EndZ=0
    g30: LineSegment [constr] StartX=233.133 StartY=0 StartZ=0 EndX=233.133 EndY=3 EndZ=0
    g31: LineSegment [constr] StartX=262.394 StartY=0 StartZ=0 EndX=262.394 EndY=3 EndZ=0
    g32: LineSegment [constr] StartX=166.748 StartY=15.0188 StartZ=0 EndX=167.748 EndY=15.0287 EndZ=0
    g33: LineSegment [constr] StartX=192.043 StartY=15.4771 StartZ=0 EndX=193.043 EndY=15.504 EndZ=0
    g34: LineSegment [constr] StartX=218.736 StartY=16.1094 StartZ=0 EndX=219.735 EndY=16.1295 EndZ=0
    g35: LineSegment [constr] StartX=247.514 StartY=17.1372 StartZ=0 EndX=246.515 EndY=17.086 EndZ=0
    g36: Circle CenterX=11.65 CenterY=11.65 CenterZ=0 NormalX=0 NormalY=0 NormalZ=1 AngleXU=0 Radius=8.9
    g37: Circle CenterX=29.95 CenterY=11.65 CenterZ=0 NormalX=0 NormalY=0 NormalZ=1 AngleXU=0 Radius=8.9
    g38: Circle CenterX=48.5476 CenterY=11.95 CenterZ=0 NormalX=0 NormalY=0 NormalZ=1 AngleXU=0 Radius=8.3
    g39: Circle CenterX=67.6465 CenterY=12.15 CenterZ=0 NormalX=0 NormalY=0 NormalZ=1 AngleXU=0 Radius=8.6
    g40: Circle CenterX=87.6825 CenterY=12.9 CenterZ=0 NormalX=0 NormalY=0 NormalZ=1 AngleXU=0 Radius=9.3
    g41: Circle CenterX=108.928 CenterY=13.35 CenterZ=0 NormalX=0 NormalY=0 NormalZ=1 AngleXU=0 Radius=9.8
    g42: Circle CenterX=131.122 CenterY=13.85 CenterZ=0 NormalX=0 NormalY=0 NormalZ=1 AngleXU=0 Radius=9.85
    g43: Circle CenterX=154.849 CenterY=14.9 CenterZ=0 NormalX=0 NormalY=0 NormalZ=1 AngleXU=0 Radius=10.85
    g44: Circle CenterX=179.898 CenterY=15.15 CenterZ=0 NormalX=0 NormalY=0 NormalZ=1 AngleXU=0 Radius=11.85
    g45: Circle CenterX=205.888 CenterY=15.85 CenterZ=0 NormalX=0 NormalY=0 NormalZ=1 AngleXU=0 Radius=11.85
    g46: Circle CenterX=233.133 CenterY=16.4 CenterZ=0 NormalX=0 NormalY=0 NormalZ=1 AngleXU=0 Radius=12.35
    g47: Circle CenterX=262.394 CenterY=17.9 CenterZ=0 NormalX=0 NormalY=0 NormalZ=1 AngleXU=0 Radius=13.35
    g48: LineSegment [constr] StartX=277.294 StartY=17.9 StartZ=0 EndX=280.294 EndY=17.9 EndZ=0
  constraints (161):
    c: PointOnObject(g8,g0)
    c: PointOnObject(g8,g1)
    c: PointOnObject(g9,g1)
    c: PointOnObject(g9,g2)
    c: PointOnObject(g10,g2)
    c: PointOnObject(g10,g3)
    c: PointOnObject(g11,g3)
    c: PointOnObject(g11,g4)
    c: PointOnObject(g12,g4)
    c: PointOnObject(g12,g5)
    c: PointOnObject(g13,g5)
    c: PointOnObject(g13,g6)
    c: PointOnObject(g14,g6)
    c: PointOnObject(g14,g7)
    c: Perpendicular(g0,g8)
    c: Perpendicular(g1,g8)
    c: Perpendicular(g1,g9)
    c: Perpendicular(g2,g9)
    c: Perpendicular(g2,g10)
    c: Perpendicular(g3,g10)
    c: Perpendicular(g3,g11)
    c: Perpendicular(g4,g11)
    c: Perpendicular(g4,g12)
    c: Perpendicular(g5,g12)
    c: Perpendicular(g5,g13)
    c: Perpendicular(g6,g13)
    c: Perpendicular(g6,g14)
    c: Perpendicular(g7,g14)
    c: Equal(g8,g9)
    c: Equal(g9,g10)
    c: Equal(g10,g11)
    c: Equal(g11,g12)
    c: Equal(g12,g13)
    c: Equal(g13,g14)
    c: Distance(g8) = 1
    c: PointOnObject(g15,g-1)
    c: PointOnObject(g15,g0)
    c: Vertical(g15)
    c: PointOnObject(g16,g-1)
    c: PointOnObject(g16,g1)
    c: Vertical(g16)
    c: PointOnObject(g17,g-1)
    c: PointOnObject(g17,g2)
    c: Vertical(g17)
    c: PointOnObject(g18,g-1)
    c: PointOnObject(g18,g3)
    c: Vertical(g18)
    c: PointOnObject(g19,g-1)
    c: PointOnObject(g19,g4)
    c: Vertical(g19)
    c: PointOnObject(g20,g-1)
    c: PointOnObject(g20,g5)
    c: Vertical(g20)
    c: PointOnObject(g21,g-1)
    c: PointOnObject(g21,g6)
    c: Vertical(g21)
    c: PointOnObject(g22,g-1)
    c: PointOnObject(g22,g7)
    c: Vertical(g22)
    c: Equal(g22,g21)
    c: Equal(g21,g20)
    c: Equal(g20,g19)
    c: Equal(g19,g18)
    c: Equal(g18,g17)
    c: Equal(g17,g15)
    c: Equal(g15,g16)
    c: Distance(g15) = 3
    c: PointOnObject(g23,g0)
    c: PointOnObject(g23,g-2)
    c: Horizontal(g23)
    c: DistanceX(g23,g23) = 3
    c: Perpendicular(g0,g23)
    c: Perpendicular(g0,g15)
    c: Perpendicular(g1,g16)
    c: Perpendicular(g2,g17)
    c: Perpendicular(g3,g18)
    c: Perpendicular(g4,g19)
    c: Perpendicular(g5,g20)
    c: Perpendicular(g6,g21)
    c: Perpendicular(g7,g22)
    c: Diameter(g0) = 17.3
    c: Diameter(g1) = 17.3
    c: Diameter(g2) = 17.9
    c: Diameter(g3) = 18.3
    c: Diameter(g4) = 19.8
    c: Diameter(g5) = 20.7
    c: Diameter(g6) = 21.7
    c: Diameter(g7) = 23.8
    c: PointOnObject(g28,g-1)
    c: PointOnObject(g28,g24)
    c: PointOnObject(g29,g-1)
    c: PointOnObject(g29,g25)
    c: Vertical(g29)
    c: PointOnObject(g30,g-1)
    c: PointOnObject(g30,g26)
    c: Vertical(g30)
    c: PointOnObject(g31,g-1)
    c: PointOnObject(g31,g27)
    c: Vertical(g31)
    c: Vertical(g28)
    c: Perpendicular(g24,g28)
    c: Perpendicular(g25,g29)
    c: Perpendicular(g26,g30)
    c: Perpendicular(g27,g31)
    c: PointOnObject(g32,g7)
    c: PointOnObject(g32,g24)
    c: Perpendicular(g7,g32)
    c: Perpendicular(g24,g32)
    c: PointOnObject(g33,g24)
    c: PointOnObject(g33,g25)
    c: Perpendicular(g24,g33)
    c: Perpendicular(g25,g33)
    c: PointOnObject(g34,g25)
    c: PointOnObject(g34,g26)
    c: Perpendicular(g26,g34)
    c: Perpendicular(g25,g34)
    c: Equal(g34,g33)
    c: Equal(g33,g32)
    c: Equal(g32,g14)
    c: PointOnObject(g35,g27)
    c: PointOnObject(g35,g26)
    c: Perpendicular(g26,g35)
    c: Perpendicular(g27,g35)
    c: Equal(g34,g35)
    c: Equal(g31,g30)
    c: Equal(g30,g29)
    c: Equal(g29,g28)
    c: Equal(g28,g22)
    c: Diameter(g24) = 24.3
    c: Diameter(g25) = 25.7
    c: Diameter(g26) = 26.8
    c: Diameter(g27) = 29.8
    c: Coincident(g36,g0)
    c: Coincident(g37,g1)
    c: Coincident(g38,g2)
    c: Coincident(g39,g3)
    c: Coincident(g40,g4)
    c: Coincident(g41,g5)
    c: Coincident(g42,g6)
    c: Coincident(g43,g7)
    c: Coincident(g44,g24)
    c: Coincident(g45,g25)
    c: Coincident(g46,g26)
    c: Coincident(g47,g27)
    c: Diameter(g36) = 17.8
    c: Diameter(g37) = 17.8
    c: Diameter(g38) = 16.6
    c: Diameter(g39) = 17.2
    c: Diameter(g40) = 18.6
    c: Diameter(g41) = 19.6
    c: Diameter(g42) = 19.7
    c: Diameter(g43) = 21.7
    c: Diameter(g44) = 23.7
    c: Diameter(g45) = 23.7
    c: Diameter(g46) = 24.7
    c: Diameter(g47) = 26.7
    c: PointOnObject(g48,g27)
    c: Perpendicular(g27,g48)
    c: Horizontal(g48)
    c: Equal(g48,g23)
    c: DistanceX(g-1,g48) = 280.294  'width3_8'
FEATURE [PartDesign::Pocket] Pocket010
  BaseFeature = -> Pad038
  Direction = (0,0,-1)
  Length = 11.4
  Length2 = 5
  Profile = -> Sketch013
  ReferenceAxis = -> Sketch013 [N_Axis]
  Refine = true
  SideType = 0
  Suppressed = false
  Type = 0
  Type2 = 0
FEATURE [Sketcher::SketchObject] Sketch014
  ArcFitTolerance = 1e-06
  AttachmentSupport = -> [Pocket010]
  ExternalGeometry = -> [Pocket010]
  ExternalTypes = [0]
  FullyConstrained = true
  MakeInternals = false
  MapMode = 5
  Placement = pos=(0,0,30) rot=(0,0,1;0rad)
  _ExternalGeoVersion = 0
  sketch-geometry (4):
    g0: LineSegment StartX=11.7248 StartY=8.65093 StartZ=0 EndX=11.5752 EndY=14.6491 EndZ=0
    g1: LineSegment StartX=262.319 StartY=20.8991 StartZ=0 EndX=262.469 EndY=14.9009 EndZ=0
    g2: LineSegment StartX=262.319 StartY=20.8991 StartZ=0 EndX=11.5752 EndY=14.6491 EndZ=0
    g3: LineSegment StartX=11.7248 StartY=8.65093 StartZ=0 EndX=262.469 EndY=14.9009 EndZ=0
  constraints (10):
    c: Symmetric(g0,g0,g-3)
    c: Coincident(g2,g1)
    c: Coincident(g2,g0)
    c: Coincident(g3,g0)
    c: Coincident(g3,g1)
    c: Perpendicular(g2,g0)
    c: Equal(g1,g0)
    c: Equal(g3,g2)
    c: Distance(g0) = 6
    c: Symmetric(g1,g1,g-4)
FEATURE [PartDesign::Pocket] Pocket011
  BaseFeature = -> Pocket010
  Direction = (0,0,-1)
  Length = 11.4
  Length2 = 5
  Profile = -> Sketch014
  ReferenceAxis = -> Sketch014 [N_Axis]
  Refine = true
  SideType = 0
  Suppressed = false
  Type = 0
  Type2 = 0
FEATURE [PartDesign::Chamfer] Chamfer005
  Angle = 45
  Base = -> Pocket011 [Edge36,Edge35,Edge38,Edge33,Edge34,Edge37,Edge42,Edge29,Edge30,Edge41,Edge40,Edge31,Edge32,Edge39,Edge28,Edge27,Edge43,Edge44,Edge26,Edge45,Edge25,Edge46,Edge47,Edge24,Edge48,Edge23,Edge21,Edge19,Edge52,Edge51,Edge50,Edge49,Edge22,Edge20,Edge18,Edge53,Edge54,Edge17,Edge55,Edge56,+5 more]
  BaseFeature = -> Pocket011
  ChamferType = 0
  FlipDirection = false
  Refine = true
  Size = 0.6
  Size2 = 1
  SupportTransform = false
  Suppressed = false
  UseAllEdges = false
FEATURE [Part::Part2DObjectPython] ShapeString032  # Draft 2D object (typed FeaturePython)
  AttachmentOffset = pos=(6,24,0) rot=(0,0,1;0rad)
  AttachmentSupport = -> [Chamfer005]
  FontFile = <userpath>/Downloads/osifont-master/osifont-master/osifont.ttf
  Fuse = false
  Justification = 6
  JustificationReference = 0
  KeepLeftMargin = false
  MakeFace = true
  MapMode = 5
  ObliqueAngle = 0
  Placement = pos=(6,24,30) rot=(0,0,1;0rad)
  ScaleToSize = true
  Size = 10
  String = 10
  Tracking = 0
FEATURE [Part::Part2DObjectPython] ShapeString033  # Draft 2D object (typed FeaturePython)
  AttachmentOffset = pos=(25,24,0) rot=(0,0,1;0rad)
  AttachmentSupport = -> [Chamfer005]
  FontFile = <userpath>/Downloads/osifont-master/osifont-master/osifont.ttf
  Fuse = false
  Justification = 6
  JustificationReference = 0
  KeepLeftMargin = false
  MakeFace = true
  MapMode = 5
  ObliqueAngle = 0
  Placement = pos=(25,24,30) rot=(0,0,1;0rad)
  ScaleToSize = true
  Size = 10
  String = 11
  Tracking = 0
FEATURE [Part::Part2DObjectPython] ShapeString034  # Draft 2D object (typed FeaturePython)
  AttachmentOffset = pos=(43,24,0) rot=(0,0,1;0rad)
  AttachmentSupport = -> [Chamfer005]
  FontFile = <userpath>/Downloads/osifont-master/osifont-master/osifont.ttf
  Fuse = false
  Justification = 6
  JustificationReference = 0
  KeepLeftMargin = false
  MakeFace = true
  MapMode = 5
  ObliqueAngle = 0
  Placement = pos=(43,24,30) rot=(0,0,1;0rad)
  ScaleToSize = true
  Size = 10
  String = 12
  Tracking = 0
FEATURE [Part::Part2DObjectPython] ShapeString035  # Draft 2D object (typed FeaturePython)
  AttachmentOffset = pos=(62.5,24,0) rot=(0,0,1;0rad)
  AttachmentSupport = -> [Chamfer005]
  FontFile = <userpath>/Downloads/osifont-master/osifont-master/osifont.ttf
  Fuse = false
  Justification = 6
  JustificationReference = 0
  KeepLeftMargin = false
  MakeFace = true
  MapMode = 5
  ObliqueAngle = 0
  Placement = pos=(62.5,24,30) rot=(0,0,1;0rad)
  ScaleToSize = true
  Size = 10
  String = 13
  Tracking = 0
FEATURE [Part::Part2DObjectPython] ShapeString036  # Draft 2D object (typed FeaturePython)
  AttachmentOffset = pos=(82,24,0) rot=(0,0,1;0rad)
  AttachmentSupport = -> [Chamfer005]
  FontFile = <userpath>/Downloads/osifont-master/osifont-master/osifont.ttf
  Fuse = false
  Justification = 6
  JustificationReference = 0
  KeepLeftMargin = false
  MakeFace = true
  MapMode = 5
  ObliqueAngle = 0
  Placement = pos=(82,24,30) rot=(0,0,1;0rad)
  ScaleToSize = true
  Size = 10
  String = 14
  Tracking = 0
FEATURE [Part::Part2DObjectPython] ShapeString037  # Draft 2D object (typed FeaturePython)
  AttachmentOffset = pos=(103,26,0) rot=(0,0,1;0rad)
  AttachmentSupport = -> [Chamfer005]
  FontFile = <userpath>/Downloads/osifont-master/osifont-master/osifont.ttf
  Fuse = false
  Justification = 6
  JustificationReference = 0
  KeepLeftMargin = false
  MakeFace = true
  MapMode = 5
  ObliqueAngle = 0
  Placement = pos=(103,26,30) rot=(0,0,1;0rad)
  ScaleToSize = true
  Size = 10
  String = 15
  Tracking = 0
FEATURE [Part::Part2DObjectPython] ShapeString038  # Draft 2D object (typed FeaturePython)
  AttachmentOffset = pos=(125,26,0) rot=(0,0,1;0rad)
  AttachmentSupport = -> [Chamfer005]
  FontFile = <userpath>/Downloads/osifont-master/osifont-master/osifont.ttf
  Fuse = false
  Justification = 6
  JustificationReference = 0
  KeepLeftMargin = false
  MakeFace = true
  MapMode = 5
  ObliqueAngle = 0
  Placement = pos=(125,26,30) rot=(0,0,1;0rad)
  ScaleToSize = true
  Size = 10
  String = 16
  Tracking = 0
FEATURE [Part::Part2DObjectPython] ShapeString039  # Draft 2D object (typed FeaturePython)
  AttachmentOffset = pos=(149,27,0) rot=(0,0,1;0rad)
  AttachmentSupport = -> [Chamfer005]
  FontFile = <userpath>/Downloads/osifont-master/osifont-master/osifont.ttf
  Fuse = false
  Justification = 6
  JustificationReference = 0
  KeepLeftMargin = false
  MakeFace = true
  MapMode = 5
  ObliqueAngle = 0
  Placement = pos=(149,27,30) rot=(0,0,1;0rad)
  ScaleToSize = true
  Size = 10
  String = 17
  Tracking = 0
FEATURE [Part::Part2DObjectPython] ShapeString040  # Draft 2D object (typed FeaturePython)
  AttachmentOffset = pos=(174,28,0) rot=(0,0,1;0rad)
  AttachmentSupport = -> [Chamfer005]
  FontFile = <userpath>/Downloads/osifont-master/osifont-master/osifont.ttf
  Fuse = false
  Justification = 6
  JustificationReference = 0
  KeepLeftMargin = false
  MakeFace = true
  MapMode = 5
  ObliqueAngle = 0
  Placement = pos=(174,28,30) rot=(0,0,1;0rad)
  ScaleToSize = true
  Size = 10
  String = 18
  Tracking = 0
FEATURE [Part::Part2DObjectPython] ShapeString041  # Draft 2D object (typed FeaturePython)
  AttachmentOffset = pos=(200,29,0) rot=(0,0,1;0rad)
  AttachmentSupport = -> [Chamfer005]
  FontFile = <userpath>/Downloads/osifont-master/osifont-master/osifont.ttf
  Fuse = false
  Justification = 6
  JustificationReference = 0
  KeepLeftMargin = false
  MakeFace = true
  MapMode = 5
  ObliqueAngle = 0
  Placement = pos=(200,29,30) rot=(0,0,1;0rad)
  ScaleToSize = true
  Size = 10
  String = 19
  Tracking = 0
FEATURE [Part::Part2DObjectPython] ShapeString042  # Draft 2D object (typed FeaturePython)
  AttachmentOffset = pos=(227,30,0) rot=(0,0,1;0rad)
  AttachmentSupport = -> [Chamfer005]
  FontFile = <userpath>/Downloads/osifont-master/osifont-master/osifont.ttf
  Fuse = false
  Justification = 6
  JustificationReference = 0
  KeepLeftMargin = false
  MakeFace = true
  MapMode = 5
  ObliqueAngle = 0
  Placement = pos=(227,30,30) rot=(0,0,1;0rad)
  ScaleToSize = true
  Size = 9
  String = 20
  Tracking = 0
FEATURE [Part::Part2DObjectPython] ShapeString043  # Draft 2D object (typed FeaturePython)
  AttachmentOffset = pos=(245,30,0) rot=(0,0,1;0rad)
  AttachmentSupport = -> [Chamfer005]
  FontFile = <userpath>/Downloads/osifont-master/osifont-master/osifont.ttf
  Fuse = false
  Justification = 6
  JustificationReference = 0
  KeepLeftMargin = false
  MakeFace = true
  MapMode = 5
  ObliqueAngle = 0
  Placement = pos=(245,30,30) rot=(0,0,1;0rad)
  ScaleToSize = true
  Size = 9
  String = 22
  Tracking = 0
FEATURE [PartDesign::Pad] Pad039
  BaseFeature = -> Chamfer005
  Direction = (0,0,1)
  Length = 1
  Length2 = 10
  Profile = -> ShapeString032
  ReferenceAxis = -> ShapeString032 [N_Axis]
  Refine = true
  SideType = 0
  Suppressed = false
  Type = 0
  Type2 = 0
FEATURE [PartDesign::Pad] Pad040
  BaseFeature = -> Pad039
  Direction = (0,0,1)
  Length = 1
  Length2 = 10
  Profile = -> ShapeString033
  ReferenceAxis = -> ShapeString033 [N_Axis]
  Refine = true
  SideType = 0
  Suppressed = false
  Type = 0
  Type2 = 0
FEATURE [PartDesign::Pad] Pad041
  BaseFeature = -> Pad040
  Direction = (0,0,1)
  Length = 1
  Length2 = 10
  Profile = -> ShapeString034
  ReferenceAxis = -> ShapeString034 [N_Axis]
  Refine = true
  SideType = 0
  Suppressed = false
  Type = 0
  Type2 = 0
FEATURE [PartDesign::Pad] Pad042
  BaseFeature = -> Pad041
  Direction = (0,0,1)
  Length = 1
  Length2 = 10
  Profile = -> ShapeString035
  ReferenceAxis = -> ShapeString035 [N_Axis]
  Refine = true
  SideType = 0
  Suppressed = false
  Type = 0
  Type2 = 0
FEATURE [PartDesign::Pad] Pad043
  BaseFeature = -> Pad042
  Direction = (0,0,1)
  Length = 1
  Length2 = 10
  Profile = -> ShapeString036
  ReferenceAxis = -> ShapeString036 [N_Axis]
  Refine = true
  SideType = 0
  Suppressed = false
  Type = 0
  Type2 = 0
FEATURE [PartDesign::Pad] Pad044
  BaseFeature = -> Pad043
  Direction = (0,0,1)
  Length = 1
  Length2 = 10
  Profile = -> ShapeString037
  ReferenceAxis = -> ShapeString037 [N_Axis]
  Refine = true
  SideType = 0
  Suppressed = false
  Type = 0
  Type2 = 0
FEATURE [PartDesign::Pad] Pad045
  BaseFeature = -> Pad044
  Direction = (0,0,1)
  Length = 1
  Length2 = 10
  Profile = -> ShapeString038
  ReferenceAxis = -> ShapeString038 [N_Axis]
  Refine = true
  SideType = 0
  Suppressed = false
  Type = 0
  Type2 = 0
FEATURE [PartDesign::Pad] Pad046
  BaseFeature = -> Pad045
  Direction = (0,0,1)
  Length = 1
  Length2 = 10
  Profile = -> ShapeString039
  ReferenceAxis = -> ShapeString039 [N_Axis]
  Refine = true
  SideType = 0
  Suppressed = false
  Type = 0
  Type2 = 0
FEATURE [PartDesign::Pad] Pad047
  BaseFeature = -> Pad046
  Direction = (0,0,1)
  Length = 1
  Length2 = 10
  Profile = -> ShapeString040
  ReferenceAxis = -> ShapeString040 [N_Axis]
  Refine = true
  SideType = 0
  Suppressed = false
  Type = 0
  Type2 = 0
FEATURE [PartDesign::Pad] Pad048
  BaseFeature = -> Pad047
  Direction = (0,0,1)
  Length = 1
  Length2 = 10
  Profile = -> ShapeString041
  ReferenceAxis = -> ShapeString041 [N_Axis]
  Refine = true
  SideType = 0
  Suppressed = false
  Type = 0
  Type2 = 0
FEATURE [PartDesign::Pad] Pad049
  BaseFeature = -> Pad048
  Direction = (0,0,1)
  Length = 1
  Length2 = 10
  Profile = -> ShapeString042
  ReferenceAxis = -> ShapeString042 [N_Axis]
  Refine = true
  SideType = 0
  Suppressed = false
  Type = 0
  Type2 = 0
FEATURE [PartDesign::Pad] Pad050
  BaseFeature = -> Pad049
  Direction = (0,0,1)
  Length = 1
  Length2 = 10
  Profile = -> ShapeString043
  ReferenceAxis = -> ShapeString043 [N_Axis]
  Refine = true
  SideType = 0
  Suppressed = false
  Type = 0
  Type2 = 0
FEATURE [PartDesign::Body] Body006  label="3_8in"
  AllowCompound = false
  Group = -> [Sketch012,Pad038,Sketch013,Pocket010,Sketch014,Pocket011,Chamfer005,ShapeString032,ShapeString033,ShapeString034,ShapeString035,ShapeString036,ShapeString037,ShapeString038,ShapeString039,ShapeString040,ShapeString041,ShapeString042,ShapeString043,Pad039,Pad040,Pad041,Pad042,Pad043,Pad044,Pad045,Pad046,Pad047,Pad048,Pad049,Pad050]
  Origin = -> Origin006
  Placement = pos=(0,-52.1,0) rot=(0,0,1;0rad)
  Tip = -> Pad050
FEATURE [Sketcher::SketchObject] Sketch015
  ArcFitTolerance = 1e-06
  AttachmentSupport = -> [XY_Plane007]
  ExternalTypes = [0]
  FullyConstrained = true
  MakeInternals = false
  MapMode = 5
  _ExternalGeoVersion = 0
  sketch-geometry (78):
    g0: Circle [constr] CenterX=8.95 CenterY=35.85 CenterZ=0 NormalX=0 NormalY=0 NormalZ=1 AngleXU=0 Radius=5.95
    g1: Circle [constr] CenterX=22.85 CenterY=35.85 CenterZ=0 NormalX=0 NormalY=0 NormalZ=1 AngleXU=0 Radius=5.95
    g2: Circle [constr] CenterX=36.75 CenterY=35.85 CenterZ=0 NormalX=0 NormalY=0 NormalZ=1 AngleXU=0 Radius=5.95
    g3: Circle [constr] CenterX=50.65 CenterY=35.85 CenterZ=0 NormalX=0 NormalY=0 NormalZ=1 AngleXU=0 Radius=5.95
    g4: Circle [constr] CenterX=64.55 CenterY=35.85 CenterZ=0 NormalX=0 NormalY=0 NormalZ=1 AngleXU=0 Radius=5.95
    g5: Circle [constr] CenterX=78.45 CenterY=35.85 CenterZ=0 NormalX=0 NormalY=0 NormalZ=1 AngleXU=0 Radius=5.95
    g6: Circle [constr] CenterX=92.4992 CenterY=36 CenterZ=0 NormalX=0 NormalY=0 NormalZ=1 AngleXU=0 Radius=6.1
    g7: Circle [constr] CenterX=107.142 CenterY=36.45 CenterZ=0 NormalX=0 NormalY=0 NormalZ=1 AngleXU=0 Radius=6.55
    g8: Circle [constr] CenterX=122.975 CenterY=37.2 CenterZ=0 NormalX=0 NormalY=0 NormalZ=1 AngleXU=0 Radius=7.3
    g9: Circle [constr] CenterX=140.212 CenterY=37.85 CenterZ=0 NormalX=0 NormalY=0 NormalZ=1 AngleXU=0 Radius=7.95
    g10: Circle [constr] CenterX=158.605 CenterY=38.35 CenterZ=0 NormalX=0 NormalY=0 NormalZ=1 AngleXU=0 Radius=8.45
    g11: Circle [constr] CenterX=178.951 CenterY=38.8 CenterZ=0 NormalX=0 NormalY=0 NormalZ=1 AngleXU=0 Radius=8.9
    g12: LineSegment [constr] StartX=3 StartY=35.85 StartZ=0 EndX=0 EndY=35.85 EndZ=0
    g13: LineSegment [constr] StartX=8.95 StartY=29.9 StartZ=0 EndX=8.95 EndY=0 EndZ=0
    g14: LineSegment [constr] StartX=22.85 StartY=29.9 StartZ=0 EndX=22.85 EndY=0 EndZ=0
    g15: LineSegment [constr] StartX=36.75 StartY=29.9 StartZ=0 EndX=36.75 EndY=0 EndZ=0
    g16: LineSegment [constr] StartX=50.65 StartY=29.9 StartZ=0 EndX=50.65 EndY=0 EndZ=0
    g17: LineSegment [constr] StartX=64.55 StartY=29.9 StartZ=0 EndX=64.55 EndY=0 EndZ=0
    g18: LineSegment [constr] StartX=78.45 StartY=29.9 StartZ=0 EndX=78.45 EndY=0 EndZ=0
    g19: LineSegment [constr] StartX=92.4992 StartY=29.9 StartZ=0 EndX=92.4992 EndY=0 EndZ=0
    g20: LineSegment [constr] StartX=107.142 StartY=29.9 StartZ=0 EndX=107.142 EndY=0 EndZ=0
    g21: LineSegment [constr] StartX=122.975 StartY=29.9 StartZ=0 EndX=122.975 EndY=0 EndZ=0
    g22: LineSegment [constr] StartX=140.212 StartY=29.9 StartZ=0 EndX=140.212 EndY=0 EndZ=0
    g23: LineSegment [constr] StartX=158.605 StartY=29.9 StartZ=0 EndX=158.605 EndY=0 EndZ=0
    g24: LineSegment [constr] StartX=178.951 StartY=29.9 StartZ=0 EndX=178.951 EndY=0 EndZ=0
    g25: LineSegment [constr] StartX=14.9 StartY=35.85 StartZ=0 EndX=16.9 EndY=35.85 EndZ=0
    g26: LineSegment [constr] StartX=28.8 StartY=35.85 StartZ=0 EndX=30.8 EndY=35.85 EndZ=0
    g27: LineSegment [constr] StartX=42.7 StartY=35.85 StartZ=0 EndX=44.7 EndY=35.85 EndZ=0
    g28: LineSegment [constr] StartX=56.6 StartY=35.85 StartZ=0 EndX=58.6 EndY=35.85 EndZ=0
    g29: LineSegment [constr] StartX=84.3997 StartY=35.9135 StartZ=0 EndX=86.3995 EndY=35.9349 EndZ=0
    g30: LineSegment [constr] StartX=70.5 StartY=35.85 StartZ=0 EndX=72.5 EndY=35.85 EndZ=0
    g31: LineSegment [constr] StartX=98.5963 StartY=36.1874 StartZ=0 EndX=100.595 EndY=36.2488 EndZ=0
    g32: LineSegment [constr] StartX=113.685 StartY=36.7599 StartZ=0 EndX=115.683 EndY=36.8546 EndZ=0
    g33: LineSegment [constr] StartX=130.269 StartY=37.4751 StartZ=0 EndX=132.268 EndY=37.5504 EndZ=0
    g34: LineSegment [constr] StartX=148.159 StartY=38.066 StartZ=0 EndX=150.159 EndY=38.1204 EndZ=0
    g35: LineSegment [constr] StartX=167.053 StartY=38.5369 StartZ=0 EndX=170.053 EndY=38.6032 EndZ=0
    g36: LineSegment [constr] StartX=187.851 StartY=38.8 StartZ=0 EndX=190.851 EndY=38.8 EndZ=0
    g37: Circle [constr] CenterX=8.95 CenterY=8.05 CenterZ=0 NormalX=0 NormalY=0 NormalZ=1 AngleXU=0 Radius=6.05
    g38: Circle [constr] CenterX=36.75 CenterY=8.05 CenterZ=0 NormalX=0 NormalY=0 NormalZ=1 AngleXU=0 Radius=6.05
    g39: Circle [constr] CenterX=64.55 CenterY=8.05 CenterZ=0 NormalX=0 NormalY=0 NormalZ=1 AngleXU=0 Radius=6.05
    g40: Circle [constr] CenterX=78.45 CenterY=8.05 CenterZ=0 NormalX=0 NormalY=0 NormalZ=1 AngleXU=0 Radius=6.05
    g41: Circle [constr] CenterX=92.4992 CenterY=8.05 CenterZ=0 NormalX=0 NormalY=0 NormalZ=1 AngleXU=0 Radius=6.05
    g42: Circle [constr] CenterX=107.142 CenterY=8.4 CenterZ=0 NormalX=0 NormalY=0 NormalZ=1 AngleXU=0 Radius=6.4
    g43: Circle [constr] CenterX=122.975 CenterY=9.3 CenterZ=0 NormalX=0 NormalY=0 NormalZ=1 AngleXU=0 Radius=7.3
    g44: Circle [constr] CenterX=140.212 CenterY=10.05 CenterZ=0 NormalX=0 NormalY=0 NormalZ=1 AngleXU=0 Radius=8.05
    g45: Circle [constr] CenterX=178.951 CenterY=10.95 CenterZ=0 NormalX=0 NormalY=0 NormalZ=1 AngleXU=0 Radius=8.95
    g46: LineSegment [constr] StartX=8.95 StartY=2 StartZ=0 EndX=8.95 EndY=0 EndZ=0
    g47: LineSegment [constr] StartX=36.75 StartY=2 StartZ=0 EndX=36.75 EndY=0 EndZ=0
    g48: LineSegment [constr] StartX=64.55 StartY=2 StartZ=0 EndX=64.55 EndY=0 EndZ=0
    g49: LineSegment [constr] StartX=78.45 StartY=2 StartZ=0 EndX=78.45 EndY=0 EndZ=0
    g50: LineSegment [constr] StartX=92.4992 StartY=2 StartZ=0 EndX=92.4992 EndY=0 EndZ=0
    g51: LineSegment [constr] StartX=107.142 StartY=2 StartZ=0 EndX=107.142 EndY=0 EndZ=0
    g52: LineSegment [constr] StartX=122.975 StartY=2 StartZ=0 EndX=122.975 EndY=0 EndZ=0
    g53: LineSegment [constr] StartX=140.212 StartY=2 StartZ=0 EndX=140.212 EndY=0 EndZ=0
    g54: LineSegment [constr] StartX=178.951 StartY=2 StartZ=0 EndX=178.951 EndY=0 EndZ=0
    g55: LineSegment [constr] StartX=178.951 StartY=19.9 StartZ=0 EndX=178.951 EndY=29.9 EndZ=0
    g56: LineSegment [constr] StartX=178.951 StartY=47.7 StartZ=0 EndX=178.951 EndY=50.7 EndZ=0
    g57: Circle CenterX=8.95 CenterY=35.85 CenterZ=0 NormalX=0 NormalY=0 NormalZ=1 AngleXU=0 Radius=6.2
    g58: Circle CenterX=22.85 CenterY=35.85 CenterZ=0 NormalX=0 NormalY=0 NormalZ=1 AngleXU=0 Radius=6.2
    g59: Circle CenterX=36.75 CenterY=35.85 CenterZ=0 NormalX=0 NormalY=0 NormalZ=1 AngleXU=0 Radius=6.2
    g60: Circle CenterX=50.65 CenterY=35.85 CenterZ=0 NormalX=0 NormalY=0 NormalZ=1 AngleXU=0 Radius=6.2
    g61: Circle CenterX=64.55 CenterY=35.85 CenterZ=0 NormalX=0 NormalY=0 NormalZ=1 AngleXU=0 Radius=6.2
    g62: Circle CenterX=78.45 CenterY=35.85 CenterZ=0 NormalX=0 NormalY=0 NormalZ=1 AngleXU=0 Radius=6.2
    g63: Circle CenterX=92.4992 CenterY=36 CenterZ=0 NormalX=0 NormalY=0 NormalZ=1 AngleXU=0 Radius=6.35
    g64: Circle CenterX=107.142 CenterY=36.45 CenterZ=0 NormalX=0 NormalY=0 NormalZ=1 AngleXU=0 Radius=6.8
    g65: Circle CenterX=122.975 CenterY=37.2 CenterZ=0 NormalX=0 NormalY=0 NormalZ=1 AngleXU=0 Radius=6.8
    g66: Circle CenterX=140.212 CenterY=37.85 CenterZ=0 NormalX=0 NormalY=0 NormalZ=1 AngleXU=0 Radius=7.3
    g67: Circle CenterX=158.605 CenterY=38.35 CenterZ=0 NormalX=0 NormalY=0 NormalZ=1 AngleXU=0 Radius=7.85
    g68: Circle CenterX=178.951 CenterY=38.8 CenterZ=0 NormalX=0 NormalY=0 NormalZ=1 AngleXU=0 Radius=8.25
    g69: Circle CenterX=178.951 CenterY=10.95 CenterZ=0 NormalX=0 NormalY=0 NormalZ=1 AngleXU=0 Radius=9.2
    g70: Circle CenterX=140.212 CenterY=10.05 CenterZ=0 NormalX=0 NormalY=0 NormalZ=1 AngleXU=0 Radius=8.3
    g71: Circle CenterX=122.975 CenterY=9.3 CenterZ=0 NormalX=0 NormalY=0 NormalZ=1 AngleXU=0 Radius=7.55
    g72: Circle CenterX=107.142 CenterY=8.4 CenterZ=0 NormalX=0 NormalY=0 NormalZ=1 AngleXU=0 Radius=6.65
    g73: Circle CenterX=92.4992 CenterY=8.05 CenterZ=0 NormalX=0 NormalY=0 NormalZ=1 AngleXU=0 Radius=6.25
    g74: Circle CenterX=78.45 CenterY=8.05 CenterZ=0 NormalX=0 NormalY=0 NormalZ=1 AngleXU=0 Radius=6.25
    g75: Circle CenterX=64.55 CenterY=8.05 CenterZ=0 NormalX=0 NormalY=0 NormalZ=1 AngleXU=0 Radius=6.25
    g76: Circle CenterX=36.75 CenterY=8.05 CenterZ=0 NormalX=0 NormalY=0 NormalZ=1 AngleXU=0 Radius=6.25
    g77: Circle CenterX=8.95 CenterY=8.05 CenterZ=0 NormalX=0 NormalY=0 NormalZ=1 AngleXU=0 Radius=6.25
  constraints (251):
    c: PointOnObject(g12,g0)
    c: PointOnObject(g12,g-2)
    c: Horizontal(g12)
    c: PointOnObject(g13,g0)
    c: PointOnObject(g13,g-1)
    c: Vertical(g13)
    c: PointOnObject(g14,g1)
    c: PointOnObject(g14,g-1)
    c: Vertical(g14)
    c: PointOnObject(g15,g2)
    c: PointOnObject(g15,g-1)
    c: Vertical(g15)
    c: PointOnObject(g16,g3)
    c: PointOnObject(g16,g-1)
    c: Vertical(g16)
    c: PointOnObject(g17,g4)
    c: PointOnObject(g17,g-1)
    c: Vertical(g17)
    c: PointOnObject(g18,g5)
    c: PointOnObject(g18,g-1)
    c: Vertical(g18)
    c: PointOnObject(g19,g6)
    c: PointOnObject(g19,g-1)
    c: Vertical(g19)
    c: PointOnObject(g20,g7)
    c: PointOnObject(g20,g-1)
    c: Vertical(g20)
    c: PointOnObject(g21,g8)
    c: PointOnObject(g21,g-1)
    c: Vertical(g21)
    c: PointOnObject(g22,g9)
    c: PointOnObject(g22,g-1)
    c: Vertical(g22)
    c: PointOnObject(g23,g10)
    c: PointOnObject(g23,g-1)
    c: Vertical(g23)
    c: PointOnObject(g24,g11)
    c: PointOnObject(g24,g-1)
    c: Vertical(g24)
    c: PointOnObject(g25,g0)
    c: PointOnObject(g25,g1)
    c: PointOnObject(g26,g1)
    c: PointOnObject(g26,g2)
    c: PointOnObject(g27,g2)
    c: PointOnObject(g27,g3)
    c: PointOnObject(g28,g3)
    c: PointOnObject(g28,g4)
    c: PointOnObject(g29,g5)
    c: PointOnObject(g29,g6)
    c: PointOnObject(g30,g4)
    c: PointOnObject(g30,g5)
    c: PointOnObject(g31,g6)
    c: PointOnObject(g31,g7)
    c: PointOnObject(g32,g7)
    c: PointOnObject(g32,g8)
    c: PointOnObject(g33,g8)
    c: PointOnObject(g33,g9)
    c: PointOnObject(g34,g9)
    c: PointOnObject(g34,g10)
    c: Perpendicular(g0,g12)
    c: Perpendicular(g0,g13)
    c: Perpendicular(g0,g25)
    c: Perpendicular(g1,g25)
    c: Perpendicular(g1,g14)
    c: Perpendicular(g1,g26)
    c: Perpendicular(g2,g26)
    c: Perpendicular(g2,g15)
    c: Perpendicular(g2,g27)
    c: Perpendicular(g3,g27)
    c: Perpendicular(g3,g16)
    c: Perpendicular(g3,g28)
    c: Perpendicular(g4,g28)
    c: Perpendicular(g4,g17)
    c: Perpendicular(g4,g30)
    c: Perpendicular(g5,g30)
    c: Perpendicular(g5,g18)
    c: Perpendicular(g5,g29)
    c: Perpendicular(g6,g29)
    c: Perpendicular(g6,g19)
    c: Perpendicular(g6,g31)
    c: Perpendicular(g7,g31)
    c: Perpendicular(g7,g20)
    c: Perpendicular(g7,g32)
    c: Perpendicular(g8,g32)
    c: Perpendicular(g8,g21)
    c: Perpendicular(g8,g33)
    c: Perpendicular(g9,g33)
    c: Perpendicular(g9,g22)
    c: Perpendicular(g9,g34)
    c: Perpendicular(g10,g34)
    c: Perpendicular(g10,g23)
    c: Perpendicular(g11,g24)
    c: Equal(g13,g14)
    c: Equal(g14,g15)
    c: Equal(g15,g16)
    c: Equal(g16,g17)
    c: Equal(g17,g18)
    c: Equal(g18,g19)
    c: Equal(g19,g20)
    c: Equal(g20,g21)
    c: Equal(g21,g22)
    c: Equal(g22,g23)
    c: Equal(g23,g24)
    c: Equal(g34,g33)
    c: Equal(g33,g32)
    c: Equal(g32,g31)
    c: Equal(g31,g29)
    c: Equal(g29,g30)
    c: Equal(g30,g28)
    c: Equal(g28,g27)
    c: Equal(g27,g26)
    c: Equal(g26,g25)
    c: DistanceX(g12,g12) = 3
    c: Diameter(g0) = 11.9
    c: Distance(g25) = 2
    c: Diameter(g1) = 11.9
    c: Diameter(g2) = 11.9
    c: Diameter(g3) = 11.9
    c: Diameter(g4) = 11.9
    c: Diameter(g5) = 11.9
    c: Diameter(g6) = 12.2
    c: Diameter(g7) = 13.1
    c: Diameter(g8) = 14.6
    c: Diameter(g9) = 15.9
    c: Diameter(g10) = 16.9
    c: Diameter(g11) = 17.8
    c: PointOnObject(g35,g10)
    c: PointOnObject(g35,g11)
    c: Perpendicular(g10,g35)
    c: Perpendicular(g11,g35)
    c: PointOnObject(g36,g11)
    c: Horizontal(g36)
    c: Perpendicular(g11,g36)
    c: Equal(g36,g12)
    c: PointOnObject(g37,g13)
    c: PointOnObject(g38,g15)
    c: PointOnObject(g39,g17)
    c: PointOnObject(g40,g18)
    c: PointOnObject(g41,g19)
    c: PointOnObject(g42,g20)
    c: PointOnObject(g43,g21)
    c: PointOnObject(g44,g22)
    c: PointOnObject(g45,g24)
    c: PointOnObject(g46,g37)
    c: PointOnObject(g46,g-1)
    c: Vertical(g46)
    c: PointOnObject(g47,g38)
    c: PointOnObject(g47,g-1)
    c: Vertical(g47)
    c: PointOnObject(g48,g39)
    c: PointOnObject(g48,g-1)
    c: Vertical(g48)
    c: PointOnObject(g49,g40)
    c: PointOnObject(g49,g-1)
    c: Vertical(g49)
    c: PointOnObject(g50,g41)
    c: PointOnObject(g50,g-1)
    c: Vertical(g50)
    c: PointOnObject(g51,g42)
    c: PointOnObject(g51,g-1)
    c: Vertical(g51)
    c: PointOnObject(g52,g43)
    c: PointOnObject(g52,g-1)
    c: Vertical(g52)
    c: PointOnObject(g53,g44)
    c: PointOnObject(g53,g-1)
    c: Vertical(g53)
    c: PointOnObject(g54,g45)
    c: PointOnObject(g54,g-1)
    c: Vertical(g54)
    c: Equal(g54,g53)
    c: Equal(g53,g52)
    c: Equal(g52,g51)
    c: Equal(g51,g50)
    c: Equal(g50,g49)
    c: Equal(g49,g48)
    c: Equal(g48,g47)
    c: Equal(g47,g46)
    c: DistanceY(g46,g46) = 2
    c: Perpendicular(g37,g46)
    c: Perpendicular(g38,g47)
    c: Perpendicular(g39,g48)
    c: Perpendicular(g40,g49)
    c: Perpendicular(g41,g50)
    c: Perpendicular(g42,g51)
    c: Perpendicular(g44,g53)
    c: Perpendicular(g45,g54)
    c: Diameter(g37) = 12.1
    c: Diameter(g38) = 12.1
    c: Diameter(g39) = 12.1
    c: Diameter(g40) = 12.1
    c: Diameter(g41) = 12.1
    c: Diameter(g42) = 12.8
    c: Diameter(g43) = 14.6
    c: Diameter(g44) = 16.1
    c: Diameter(g45) = 17.9
    c: Equal(g35,g36)
    c: PointOnObject(g55,g45)
    c: PointOnObject(g55,g11)
    c: Vertical(g55)
    c: DistanceY(g55,g55) = 10
    c: Perpendicular(g45,g55)
    c: Perpendicular(g43,g52)
    c: PointOnObject(g56,g11)
    c: Vertical(g56)
    c: Equal(g56,g36)
    c: Perpendicular(g11,g56)
    c: DistanceX(g12,g36) = 190.851  'width_1_4'
    c: DistanceY(g24,g56) = 50.7  'height_1_4'
    c: Coincident(g57,g0)
    c: Coincident(g58,g1)
    c: Coincident(g59,g2)
    c: Coincident(g60,g3)
    c: Coincident(g61,g4)
    c: Coincident(g62,g5)
    c: Coincident(g63,g6)
    c: Coincident(g64,g7)
    c: Coincident(g65,g8)
    c: Coincident(g66,g9)
    c: Coincident(g67,g10)
    c: Coincident(g68,g11)
    c: Coincident(g69,g45)
    c: Coincident(g70,g44)
    c: Coincident(g71,g43)
    c: Coincident(g72,g42)
    c: Coincident(g73,g41)
    c: Coincident(g74,g40)
    c: Coincident(g75,g39)
    c: Coincident(g76,g38)
    c: Coincident(g77,g37)
    c: Diameter(g57) = 12.4
    c: Diameter(g58) = 12.4
    c: Diameter(g59) = 12.4
    c: Diameter(g60) = 12.4
    c: Diameter(g61) = 12.4
    c: Diameter(g62) = 12.4
    c: Diameter(g63) = 12.7
    c: Diameter(g64) = 13.6
    c: Diameter(g65) = 13.6
    c: Diameter(g66) = 14.6
    c: Diameter(g67) = 15.7
    c: Diameter(g68) = 16.5
    c: Diameter(g77) = 12.5
    c: Diameter(g76) = 12.5
    c: Diameter(g75) = 12.5
    c: Diameter(g74) = 12.5
    c: Diameter(g73) = 12.5
    c: Diameter(g72) = 13.3
    c: Diameter(g71) = 15.1
    c: Diameter(g70) = 16.6
    c: Diameter(g69) = 18.4
FEATURE [Sketcher::SketchObject] Sketch016
  ArcFitTolerance = 1e-06
  AttachmentSupport = -> [XY_Plane007]
  ExternalTypes = [0]
  FullyConstrained = true
  MakeInternals = false
  MapMode = 5
  _ExternalGeoVersion = 0
  expr: Constraints[10] = Sketch015.Constraints.width_1_4
  expr: Constraints[9] = Sketch015.Constraints.height_1_4
  sketch-geometry (4):
    g0: LineSegment StartX=0 StartY=0 StartZ=0 EndX=190.851 EndY=0 EndZ=0
    g1: LineSegment StartX=190.851 StartY=0 StartZ=0 EndX=190.851 EndY=50.7 EndZ=0
    g2: LineSegment StartX=190.851 StartY=50.7 StartZ=0 EndX=0 EndY=50.7 EndZ=0
    g3: LineSegment StartX=0 StartY=50.7 StartZ=0 EndX=0 EndY=0 EndZ=0
  constraints (11):
    c: Coincident(g0,g1)
    c: Coincident(g1,g2)
    c: Coincident(g2,g3)
    c: Coincident(g3,g0)
    c: Horizontal(g0)
    c: Horizontal(g2)
    c: Vertical(g1)
    c: Vertical(g3)
    c: Coincident(g0,g-1)
    c: DistanceY(g1,g1) = 50.7
    c: DistanceX(g2,g2) = 190.851
FEATURE [PartDesign::Pad] Pad051
  Direction = (0,0,1)
  Length = 30
  Length2 = 10
  Profile = -> Sketch016
  ReferenceAxis = -> Sketch016 [N_Axis]
  Refine = true
  Reversed = true
  SideType = 0
  Suppressed = false
  Type = 0
  Type2 = 0
FEATURE [PartDesign::Pocket] Pocket012
  BaseFeature = -> Pad051
  Direction = (0,0,-1)
  Length = 9
  Length2 = 5
  Profile = -> Sketch015
  ReferenceAxis = -> Sketch015 [N_Axis]
  Refine = true
  SideType = 0
  Suppressed = false
  Type = 0
  Type2 = 0
FEATURE [PartDesign::Pocket] Pocket013
  BaseFeature = -> Pocket012
  Direction = (0,0,-1)
  Length = 29
  Length2 = 5
  Profile = -> Pocket012 [Edge12,Edge13,Edge14,Edge15,Edge16,Edge17,Edge18,Edge19,Edge20]
  Refine = true
  SideType = 0
  Suppressed = false
  Type = 0
  Type2 = 0
FEATURE [Sketcher::SketchObject] Sketch017
  ArcFitTolerance = 1e-06
  AttachmentSupport = -> [Pocket013]
  ExternalGeometry = -> [Pocket013]
  ExternalTypes = [0]
  FullyConstrained = true
  MakeInternals = false
  MapMode = 5
  _ExternalGeoVersion = 0
  sketch-geometry (4):
    g0: LineSegment StartX=8.97505 StartY=34.3502 StartZ=0 EndX=8.92495 EndY=37.3498 EndZ=0
    g1: LineSegment StartX=158.58 StartY=39.8498 StartZ=0 EndX=158.631 EndY=36.8502 EndZ=0
    g2: LineSegment StartX=8.92495 StartY=37.3498 StartZ=0 EndX=158.58 EndY=39.8498 EndZ=0
    g3: LineSegment StartX=158.631 StartY=36.8502 StartZ=0 EndX=8.97505 EndY=34.3502 EndZ=0
  constraints (10):
    c: Symmetric(g0,g0,g-3)
    c: Parallel(g1,g0)
    c: Coincident(g2,g0)
    c: Coincident(g2,g1)
    c: Coincident(g0,g3)
    c: Coincident(g3,g1)
    c: Perpendicular(g0,g3)
    c: Perpendicular(g2,g1)
    c: Distance(g0) = 3
    c: Symmetric(g1,g1,g-4)
FEATURE [PartDesign::Pocket] Pocket014
  BaseFeature = -> Pocket013
  Direction = (0,0,-1)
  Length = 9
  Length2 = 5
  Profile = -> Sketch017
  ReferenceAxis = -> Sketch017 [N_Axis]
  Refine = true
  SideType = 0
  Suppressed = false
  Type = 0
  Type2 = 0
FEATURE [Sketcher::SketchObject] Sketch018
  ArcFitTolerance = 1e-06
  AttachmentSupport = -> [Pocket014]
  ExternalGeometry = -> [Pocket014]
  ExternalTypes = [0]
  FullyConstrained = true
  MakeInternals = false
  MapMode = 5
  _ExternalGeoVersion = 0
  sketch-geometry (4):
    g0: LineSegment StartX=64.5038 StartY=9.79939 StartZ=0 EndX=64.5962 EndY=6.30061 EndZ=0
    g1: LineSegment StartX=140.259 StartY=8.30061 StartZ=0 EndX=140.166 EndY=11.7994 EndZ=0
    g2: LineSegment StartX=64.5038 StartY=9.79939 StartZ=0 EndX=140.166 EndY=11.7994 EndZ=0
    g3: LineSegment StartX=64.5962 StartY=6.30061 StartZ=0 EndX=140.259 EndY=8.30061 EndZ=0
  constraints (10):
    c: Symmetric(g0,g0,g-3)
    c: Symmetric(g1,g1,g-4)
    c: Coincident(g2,g0)
    c: Coincident(g2,g1)
    c: Coincident(g3,g0)
    c: Coincident(g3,g1)
    c: Parallel(g0,g1)
    c: Equal(g1,g0)
    c: Perpendicular(g1,g3)
    c: Distance(g0) = 3.5
FEATURE [PartDesign::Pocket] Pocket015
  BaseFeature = -> Pocket014
  Direction = (0,0,-1)
  Length = 29
  Length2 = 5
  Profile = -> Sketch018
  ReferenceAxis = -> Sketch018 [N_Axis]
  Refine = true
  SideType = 0
  Suppressed = false
  Type = 0
  Type2 = 0
FEATURE [PartDesign::Chamfer] Chamfer006
  Angle = 45
  Base = -> Pocket015 [Edge8,Edge9,Edge10,Edge30,Edge11,Edge29,Edge12,Edge13,Edge28,Edge27,Edge14,Edge16,Edge15,Edge26,Edge25,Edge24,Edge17,Edge18,Edge23,Edge19,Edge22,Edge21,Edge20,Edge3,Edge72,Edge71,Edge70,Edge69,Edge68,Edge66,Edge67,Edge64,Edge65,Edge63,Edge62,Edge60,Edge61,Edge59,Edge58,Edge56,+26 more]
  BaseFeature = -> Pocket015
  ChamferType = 0
  FlipDirection = false
  Refine = true
  Size = 0.5
  Size2 = 1
  SupportTransform = false
  Suppressed = false
  UseAllEdges = false
FEATURE [Part::Part2DObjectPython] ShapeString044  # Draft 2D object (typed FeaturePython)
  AttachmentOffset = pos=(6,20,0) rot=(0,0,1;0rad)
  AttachmentSupport = -> [Chamfer006]
  FontFile = <userpath>/Downloads/osifont-master/osifont-master/osifont.ttf
  Fuse = false
  Justification = 6
  JustificationReference = 0
  KeepLeftMargin = false
  MakeFace = true
  MapMode = 5
  ObliqueAngle = 0
  Placement = pos=(6,20,0) rot=(0,0,1;0rad)
  ScaleToSize = true
  Size = 8
  String = 4
  Tracking = 0
FEATURE [Part::Part2DObjectPython] ShapeString045  # Draft 2D object (typed FeaturePython)
  AttachmentOffset = pos=(16.5,20,0) rot=(0,0,1;0rad)
  AttachmentSupport = -> [Chamfer006]
  FontFile = <userpath>/Downloads/osifont-master/osifont-master/osifont.ttf
  Fuse = false
  Justification = 6
  JustificationReference = 0
  KeepLeftMargin = false
  MakeFace = true
  MapMode = 5
  ObliqueAngle = 0
  Placement = pos=(16.5,20,0) rot=(0,0,1;0rad)
  ScaleToSize = true
  Size = 8
  String = 4.5
  Tracking = 0
FEATURE [Part::Part2DObjectPython] ShapeString046  # Draft 2D object (typed FeaturePython)
  AttachmentOffset = pos=(35,20,0) rot=(0,0,1;0rad)
  AttachmentSupport = -> [Chamfer006]
  FontFile = <userpath>/Downloads/osifont-master/osifont-master/osifont.ttf
  Fuse = false
  Justification = 6
  JustificationReference = 0
  KeepLeftMargin = false
  MakeFace = true
  MapMode = 5
  ObliqueAngle = 0
  Placement = pos=(35,20,0) rot=(0,0,1;0rad)
  ScaleToSize = true
  Size = 8
  String = 5
  Tracking = 0
FEATURE [Part::Part2DObjectPython] ShapeString047  # Draft 2D object (typed FeaturePython)
  AttachmentOffset = pos=(45,20,0) rot=(0,0,1;0rad)
  AttachmentSupport = -> [Chamfer006]
  FontFile = <userpath>/Downloads/osifont-master/osifont-master/osifont.ttf
  Fuse = false
  Justification = 6
  JustificationReference = 0
  KeepLeftMargin = false
  MakeFace = true
  MapMode = 5
  ObliqueAngle = 0
  Placement = pos=(45,20,0) rot=(0,0,1;0rad)
  ScaleToSize = true
  Size = 8
  String = 5.5
  Tracking = 0
FEATURE [Part::Part2DObjectPython] ShapeString048  # Draft 2D object (typed FeaturePython)
  AttachmentOffset = pos=(62.5,20,0) rot=(0,0,1;0rad)
  AttachmentSupport = -> [Chamfer006]
  FontFile = <userpath>/Downloads/osifont-master/osifont-master/osifont.ttf
  Fuse = false
  Justification = 6
  JustificationReference = 0
  KeepLeftMargin = false
  MakeFace = true
  MapMode = 5
  ObliqueAngle = 0
  Placement = pos=(62.5,20,0) rot=(0,0,1;0rad)
  ScaleToSize = true
  Size = 8
  String = 6
  Tracking = 0
FEATURE [Part::Part2DObjectPython] ShapeString049  # Draft 2D object (typed FeaturePython)
  AttachmentOffset = pos=(76,20,0) rot=(0,0,1;0rad)
  AttachmentSupport = -> [Chamfer006]
  FontFile = <userpath>/Downloads/osifont-master/osifont-master/osifont.ttf
  Fuse = false
  Justification = 6
  JustificationReference = 0
  KeepLeftMargin = false
  MakeFace = true
  MapMode = 5
  ObliqueAngle = 0
  Placement = pos=(76,20,0) rot=(0,0,1;0rad)
  ScaleToSize = true
  Size = 8
  String = 7
  Tracking = 0
FEATURE [Part::Part2DObjectPython] ShapeString050  # Draft 2D object (typed FeaturePython)
  AttachmentOffset = pos=(90,20,0) rot=(0,0,1;0rad)
  AttachmentSupport = -> [Chamfer006]
  FontFile = <userpath>/Downloads/osifont-master/osifont-master/osifont.ttf
  Fuse = false
  Justification = 6
  JustificationReference = 0
  KeepLeftMargin = false
  MakeFace = true
  MapMode = 5
  ObliqueAngle = 0
  Placement = pos=(90,20,0) rot=(0,0,1;0rad)
  ScaleToSize = true
  Size = 8
  String = 8
  Tracking = 0
FEATURE [Part::Part2DObjectPython] ShapeString051  # Draft 2D object (typed FeaturePython)
  AttachmentOffset = pos=(105,20,0) rot=(0,0,1;0rad)
  AttachmentSupport = -> [Chamfer006]
  FontFile = <userpath>/Downloads/osifont-master/osifont-master/osifont.ttf
  Fuse = false
  Justification = 6
  JustificationReference = 0
  KeepLeftMargin = false
  MakeFace = true
  MapMode = 5
  ObliqueAngle = 0
  Placement = pos=(105,20,0) rot=(0,0,1;0rad)
  ScaleToSize = true
  Size = 8
  String = 9
  Tracking = 0
FEATURE [Part::Part2DObjectPython] ShapeString052  # Draft 2D object (typed FeaturePython)
  AttachmentOffset = pos=(119,20,0) rot=(0,0,1;0rad)
  AttachmentSupport = -> [Chamfer006]
  FontFile = <userpath>/Downloads/osifont-master/osifont-master/osifont.ttf
  Fuse = false
  Justification = 6
  JustificationReference = 0
  KeepLeftMargin = false
  MakeFace = true
  MapMode = 5
  ObliqueAngle = 0
  Placement = pos=(119,20,0) rot=(0,0,1;0rad)
  ScaleToSize = true
  Size = 8
  String = 10
  Tracking = 0
FEATURE [Part::Part2DObjectPython] ShapeString053  # Draft 2D object (typed FeaturePython)
  AttachmentOffset = pos=(137,21,0) rot=(0,0,1;0rad)
  AttachmentSupport = -> [Chamfer006]
  FontFile = <userpath>/Downloads/osifont-master/osifont-master/osifont.ttf
  Fuse = false
  Justification = 6
  JustificationReference = 0
  KeepLeftMargin = false
  MakeFace = true
  MapMode = 5
  ObliqueAngle = 0
  Placement = pos=(137,21,0) rot=(0,0,1;0rad)
  ScaleToSize = true
  Size = 8
  String = 11
  Tracking = 0
FEATURE [Part::Part2DObjectPython] ShapeString054  # Draft 2D object (typed FeaturePython)
  AttachmentOffset = pos=(154,21,0) rot=(0,0,1;0rad)
  AttachmentSupport = -> [Chamfer006]
  FontFile = <userpath>/Downloads/osifont-master/osifont-master/osifont.ttf
  Fuse = false
  Justification = 6
  JustificationReference = 0
  KeepLeftMargin = false
  MakeFace = true
  MapMode = 5
  ObliqueAngle = 0
  Placement = pos=(154,21,0) rot=(0,0,1;0rad)
  ScaleToSize = true
  Size = 8
  String = 12
  Tracking = 0
FEATURE [Part::Part2DObjectPython] ShapeString055  # Draft 2D object (typed FeaturePython)
  AttachmentOffset = pos=(174.5,21,0) rot=(0,0,1;0rad)
  AttachmentSupport = -> [Chamfer006]
  FontFile = <userpath>/Downloads/osifont-master/osifont-master/osifont.ttf
  Fuse = false
  Justification = 6
  JustificationReference = 0
  KeepLeftMargin = false
  MakeFace = true
  MapMode = 5
  ObliqueAngle = 0
  Placement = pos=(174.5,21,0) rot=(0,0,1;0rad)
  ScaleToSize = true
  Size = 8
  String = 13
  Tracking = 0
FEATURE [PartDesign::Pad] Pad052
  BaseFeature = -> Chamfer006
  Direction = (0,0,1)
  Length = 1
  Length2 = 10
  Profile = -> ShapeString044
  ReferenceAxis = -> ShapeString044 [N_Axis]
  Refine = true
  SideType = 0
  Suppressed = false
  Type = 0
  Type2 = 0
FEATURE [PartDesign::Pad] Pad053
  BaseFeature = -> Pad052
  Direction = (0,0,1)
  Length = 1
  Length2 = 10
  Profile = -> ShapeString045
  ReferenceAxis = -> ShapeString045 [N_Axis]
  Refine = true
  SideType = 0
  Suppressed = false
  Type = 0
  Type2 = 0
FEATURE [PartDesign::Pad] Pad054
  BaseFeature = -> Pad053
  Direction = (0,0,1)
  Length = 1
  Length2 = 10
  Profile = -> ShapeString046
  ReferenceAxis = -> ShapeString046 [N_Axis]
  Refine = true
  SideType = 0
  Suppressed = false
  Type = 0
  Type2 = 0
FEATURE [PartDesign::Pad] Pad055
  BaseFeature = -> Pad054
  Direction = (0,0,1)
  Length = 1
  Length2 = 10
  Profile = -> ShapeString047
  ReferenceAxis = -> ShapeString047 [N_Axis]
  Refine = true
  SideType = 0
  Suppressed = false
  Type = 0
  Type2 = 0
FEATURE [PartDesign::Pad] Pad056
  BaseFeature = -> Pad055
  Direction = (0,0,1)
  Length = 1
  Length2 = 10
  Profile = -> ShapeString048
  ReferenceAxis = -> ShapeString048 [N_Axis]
  Refine = true
  SideType = 0
  Suppressed = false
  Type = 0
  Type2 = 0
FEATURE [PartDesign::Pad] Pad057
  BaseFeature = -> Pad056
  Direction = (0,0,1)
  Length = 1
  Length2 = 10
  Profile = -> ShapeString049
  ReferenceAxis = -> ShapeString049 [N_Axis]
  Refine = true
  SideType = 0
  Suppressed = false
  Type = 0
  Type2 = 0
FEATURE [PartDesign::Pad] Pad058
  BaseFeature = -> Pad057
  Direction = (0,0,1)
  Length = 1
  Length2 = 10
  Profile = -> ShapeString050
  ReferenceAxis = -> ShapeString050 [N_Axis]
  Refine = true
  SideType = 0
  Suppressed = false
  Type = 0
  Type2 = 0
FEATURE [PartDesign::Pad] Pad059
  BaseFeature = -> Pad058
  Direction = (0,0,1)
  Length = 1
  Length2 = 10
  Profile = -> ShapeString051
  ReferenceAxis = -> ShapeString051 [N_Axis]
  Refine = true
  SideType = 0
  Suppressed = false
  Type = 0
  Type2 = 0
FEATURE [PartDesign::Pad] Pad060
  BaseFeature = -> Pad059
  Direction = (0,0,1)
  Length = 1
  Length2 = 10
  Profile = -> ShapeString052
  ReferenceAxis = -> ShapeString052 [N_Axis]
  Refine = true
  SideType = 0
  Suppressed = false
  Type = 0
  Type2 = 0
FEATURE [PartDesign::Pad] Pad061
  BaseFeature = -> Pad060
  Direction = (0,0,1)
  Length = 1
  Length2 = 10
  Profile = -> ShapeString053
  ReferenceAxis = -> ShapeString053 [N_Axis]
  Refine = true
  SideType = 0
  Suppressed = false
  Type = 0
  Type2 = 0
FEATURE [PartDesign::Pad] Pad062
  BaseFeature = -> Pad061
  Direction = (0,0,1)
  Length = 1
  Length2 = 10
  Profile = -> ShapeString054
  ReferenceAxis = -> ShapeString054 [N_Axis]
  Refine = true
  SideType = 0
  Suppressed = false
  Type = 0
  Type2 = 0
FEATURE [PartDesign::Pad] Pad063
  BaseFeature = -> Pad062
  Direction = (0,0,1)
  Length = 1
  Length2 = 10
  Profile = -> ShapeString055
  ReferenceAxis = -> ShapeString055 [N_Axis]
  Refine = true
  SideType = 0
  Suppressed = false
  Type = 0
  Type2 = 0
FEATURE [PartDesign::Body] Body007  label="1_4in"
  AllowCompound = false
  Group = -> [Sketch015,Sketch016,Pad051,Pocket012,Pocket013,Sketch017,Pocket014,Sketch018,Pocket015,Chamfer006,ShapeString044,ShapeString045,ShapeString046,ShapeString047,ShapeString048,ShapeString049,ShapeString050,ShapeString051,ShapeString052,ShapeString053,ShapeString054,ShapeString055,Pad052,Pad053,Pad054,Pad055,Pad056,Pad057,Pad058,Pad059,Pad060,Pad061,Pad062,Pad063]
  Origin = -> Origin007
  Placement = pos=(0,-223.6,0) rot=(0,0,1;0rad)
  Tip = -> Pad063
FEATURE [App::Point] Origin008  label="Origin"
  Role = Origin
FEATURE [App::Point] Origin009  label="Origin"
  Role = Origin
FEATURE [App::Point] Origin010  label="Origin"
  Role = Origin
FEATURE [App::Point] Origin011  label="Origin"
  Role = Origin
FEATURE [App::Point] Origin012  label="Origin"
  Role = Origin
FEATURE [App::Point] Origin013  label="Origin"
  Role = Origin
FEATURE [App::Point] Origin015
  Role = Origin
FEATURE [Sketcher::SketchObject] Sketch019
  ArcFitTolerance = 1e-06
  AttachmentSupport = -> [Origin014]
  ExternalTypes = [0]
  FullyConstrained = true
  MakeInternals = false
  MapMode = 5
  _ExternalGeoVersion = 1
  sketch-geometry (4):
    g0: LineSegment StartX=0 StartY=0 StartZ=0 EndX=34 EndY=0 EndZ=0
    g1: LineSegment StartX=34 StartY=0 StartZ=0 EndX=34 EndY=80 EndZ=0
    g2: LineSegment StartX=34 StartY=80 StartZ=0 EndX=0 EndY=80 EndZ=0
    g3: LineSegment StartX=0 StartY=80 StartZ=0 EndX=0 EndY=0 EndZ=0
  constraints (11):
    c: Coincident(g0,g1)
    c: Coincident(g1,g2)
    c: Coincident(g2,g3)
    c: Coincident(g3,g0)
    c: Horizontal(g0)
    c: Horizontal(g2)
    c: Vertical(g1)
    c: Vertical(g3)
    c: Coincident(g0,g-1)
    c: DistanceX(g0,g0) = 34
    c: DistanceY(g1,g1) = 80
FEATURE [PartDesign::Pad] Pad064
  Direction = (0,0,1)
  Length = 30
  Length2 = 10
  Profile = -> Sketch019
  ReferenceAxis = -> Sketch019 [N_Axis]
  Refine = true
  SideType = 0
  Suppressed = false
  Type = 0
  Type2 = 0
FEATURE [Sketcher::SketchObject] Sketch020
  ArcFitTolerance = 1e-06
  AttachmentSupport = -> [Pad064]
  ExternalTypes = [0]
  FullyConstrained = true
  MakeInternals = false
  MapMode = 5
  Placement = pos=(0,0,30) rot=(0,0,1;0rad)
  _ExternalGeoVersion = 1
  sketch-geometry (2):
    g0: Circle CenterX=17 CenterY=52.25 CenterZ=0 NormalX=0 NormalY=0 NormalZ=1 AngleXU=0 Radius=15.25
    g1: LineSegment [constr] StartX=17 StartY=37 StartZ=0 EndX=17 EndY=0 EndZ=0
  constraints (7):
    c: Diameter(g0) = 30.5
    c: PointOnObject(g1,g0)
    c: PointOnObject(g1,g-1)
    c: Vertical(g1)
    c: Perpendicular(g0,g1)
    c: DistanceX(g-1,g1) = 17
    c: DistanceY(g1,g1) = 37
FEATURE [PartDesign::Pocket] Pocket016
  BaseFeature = -> Pad064
  Direction = (0,0,-1)
  Length = 20
  Length2 = 5
  Profile = -> Sketch020
  ReferenceAxis = -> Sketch020 [N_Axis]
  Refine = true
  SideType = 0
  Suppressed = false
  Type = 0
  Type2 = 0
FEATURE [PartDesign::Fillet] Fillet001
  Base = -> Pocket016 [Edge5,Edge2,Edge1,Edge8,Edge11,Edge6,Edge9,Edge3]
  BaseFeature = -> Pocket016
  Radius = 2
  Refine = true
  SupportTransform = false
  Suppressed = false
  UseAllEdges = false
FEATURE [PartDesign::Fillet] Fillet002
  Base = -> Fillet001 [Edge12]
  BaseFeature = -> Fillet001
  Radius = 0.5
  Refine = true
  SupportTransform = false
  Suppressed = false
  UseAllEdges = false
FEATURE [Part::Part2DObjectPython] ShapeString056  # Draft 2D object (typed FeaturePython)
  AttachmentOffset = pos=(12.5,70,0) rot=(0,0,1;0rad)
  AttachmentSupport = -> [Fillet002]
  FontFile = <path>
  Fuse = false
  Justification = 6
  JustificationReference = 0
  KeepLeftMargin = false
  MakeFace = true
  MapMode = 5
  ObliqueAngle = 0
  Placement = pos=(12.5,70,30) rot=(0,0,1;0rad)
  ScaleToSize = true
  Size = 9
  String = 18
  Tracking = 0
FEATURE [PartDesign::Pad] Pad065
  BaseFeature = -> Fillet002
  Direction = (0,0,1)
  Length = 1
  Length2 = 10
  Profile = -> ShapeString056
  ReferenceAxis = -> ShapeString056 [N_Axis]
  Refine = true
  SideType = 0
  Suppressed = false
  Type = 0
  Type2 = 0
FEATURE [PartDesign::Body] Body008  label="18mm_pwr_socket"
  AllowCompound = true
  Group = -> [Sketch019,Pad064,Sketch020,Pocket016,Fillet001,Fillet002,ShapeString056,Pad065]
  Origin = -> Origin014
  Tip = -> Pad065
note: 1 file-system path scrubbed to <path> (originals preserved in the JSON sidecar)
